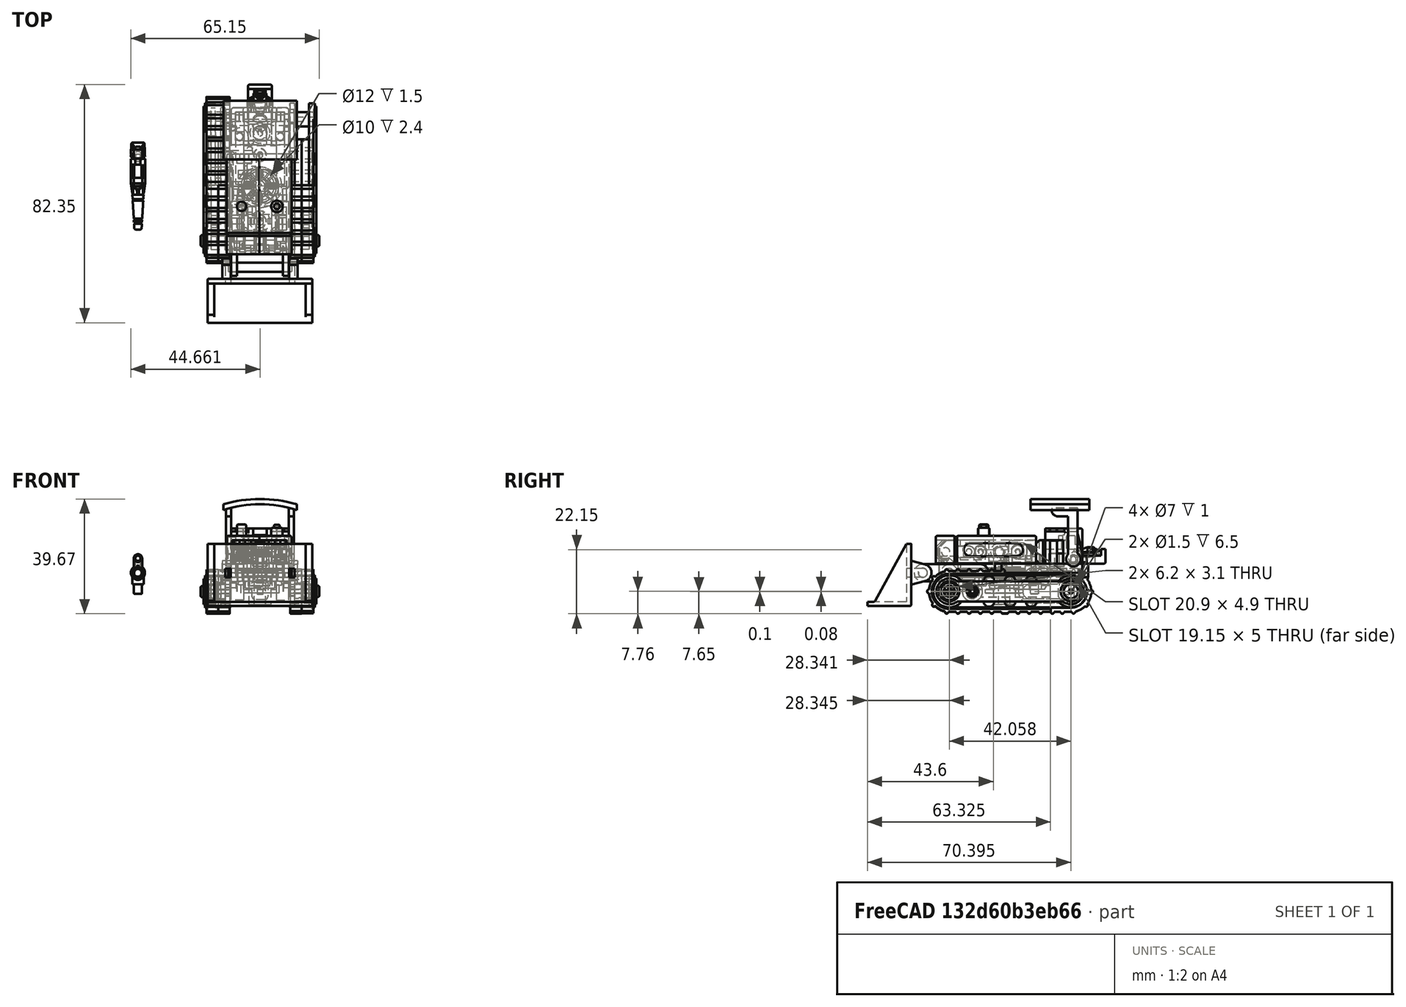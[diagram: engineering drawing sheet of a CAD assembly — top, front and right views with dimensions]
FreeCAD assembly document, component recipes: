
FREECAD ASSEMBLY — COMPONENT RECIPES ("Bonecrusher")

This assembly document has 22 components, labeled P0..P21 below (a component is one placed body or linked part). 22 of them carry a construction recipe — the FreeCAD feature program that regenerates the part from scratch, quoted from this document or its linked companion documents; the rest are supplied as boundary geometry only. No exploded tour is included for this assembly.
NOTE — document 3 of 4 of this assembly tour. The two overview renders and the header above are repeated from document 1; the component sections below continue where the previous document stopped.
COMPONENT P13 — recipe-attached ("Pre_Left_Outer_Leg", modeled in this document).
Construction recipe (the document's own serialized feature program — sketch geometry with constraints, then the solid features built on it; lengths are millimeters unless a unit is written):

FEATURE [Sketcher::SketchObject] Sketch286
  ArcFitTolerance = 1e-06
  AttachmentSupport = -> [XY_Plane026]
  FullyConstrained = true
  MakeInternals = false
  MapMode = 5
  sketch-geometry (4):
    g0: ArcOfCircle CenterX=0 CenterY=0 CenterZ=0 NormalX=0 NormalY=0 NormalZ=1 AngleXU=0 Radius=5.55 StartAngle=1.5708 EndAngle=4.71239
    g1: ArcOfCircle CenterX=42.05 CenterY=4e-16 CenterZ=0 NormalX=0 NormalY=0 NormalZ=1 AngleXU=0 Radius=5.55 StartAngle=4.71239 EndAngle=7.85398
    g2: LineSegment StartX=-3e-15 StartY=5.55 StartZ=0 EndX=42.05 EndY=5.55 EndZ=0
    g3: LineSegment StartX=-1e-15 StartY=-5.55 StartZ=0 EndX=42.05 EndY=-5.55 EndZ=0
  constraints (9):
    c: Tangent(g0,g2) = 1.5708
    c: Tangent(g0,g3) = -1.5708
    c: Tangent(g1,g2) = 1.5708
    c: Tangent(g1,g3) = -1.5708
    c: Equal(g0,g1)
    c: Horizontal(g3)
    c: Coincident(g0,g-1)
    c: DistanceX(g0,g1) = 42.05
    c: Diameter(g0) = 11.1
FEATURE [PartDesign::Pad] Pad164
  Direction = (0,0,1)
  Length = 1.6
  Length2 = 10
  Profile = -> Sketch286
  ReferenceAxis = -> Sketch286 [N_Axis]
  Refine = true
  Suppressed = false
  Type = 0
FEATURE [Sketcher::SketchObject] Sketch287
  ArcFitTolerance = 1e-06
  AttachmentSupport = -> [Pad164]
  ExternalGeometry = -> [Pad164]
  FullyConstrained = true
  MakeInternals = false
  MapMode = 5
  Placement = pos=(0,0,1.6) rot=(0,0,1;0rad)
  sketch-geometry (4):
    g0: ArcOfCircle CenterX=0 CenterY=0 CenterZ=0 NormalX=0 NormalY=0 NormalZ=1 AngleXU=0 Radius=3.5 StartAngle=1.5708 EndAngle=4.71239
    g1: ArcOfCircle CenterX=42.05 CenterY=4e-16 CenterZ=0 NormalX=0 NormalY=0 NormalZ=1 AngleXU=0 Radius=3.5 StartAngle=4.71239 EndAngle=7.85398
    g2: LineSegment StartX=-6e-16 StartY=3.5 StartZ=0 EndX=42.05 EndY=3.5 EndZ=0
    g3: LineSegment StartX=-6e-16 StartY=-3.5 StartZ=0 EndX=42.05 EndY=-3.5 EndZ=0
  constraints (8):
    c: Tangent(g0,g2) = 1.5708
    c: Tangent(g0,g3) = -1.5708
    c: Tangent(g1,g2) = 1.5708
    c: Tangent(g1,g3) = -1.5708
    c: Equal(g0,g1)
    c: Diameter(g0) = 7
    c: Coincident(g0,g-1)
    c: Coincident(g1,g-3)
FEATURE [PartDesign::Pad] Pad165
  BaseFeature = -> Pad164
  Direction = (0,0,1)
  Length = 1
  Length2 = 10
  Profile = -> Sketch287
  ReferenceAxis = -> Sketch287 [N_Axis]
  Refine = true
  Suppressed = false
  Type = 0
FEATURE [Sketcher::SketchObject] Sketch288
  ArcFitTolerance = 1e-06
  AttachmentSupport = -> [Pad165]
  ExternalGeometry = -> [Pad165]
  FullyConstrained = true
  MakeInternals = false
  MapMode = 5
  Placement = pos=(0,0,1.6) rot=(0,0,1;0rad)
  sketch-geometry (14):
    g0: Circle CenterX=42.05 CenterY=0 CenterZ=0 NormalX=0 NormalY=0 NormalZ=1 AngleXU=0 Radius=5.55
    g1: Circle CenterX=0 CenterY=0 CenterZ=0 NormalX=0 NormalY=0 NormalZ=1 AngleXU=0 Radius=5.55
    g2: ArcOfCircle CenterX=13.725 CenterY=3.5 CenterZ=0 NormalX=0 NormalY=0 NormalZ=1 AngleXU=0 Radius=1.85 StartAngle=1e-16 EndAngle=3.14159
    g3: ArcOfCircle CenterX=13.725 CenterY=-3.5 CenterZ=0 NormalX=0 NormalY=0 NormalZ=1 AngleXU=0 Radius=1.85 StartAngle=3.14159 EndAngle=6.28319
    g4: LineSegment StartX=15.575 StartY=3.5 StartZ=0 EndX=15.575 EndY=-3.5 EndZ=0
    g5: LineSegment StartX=11.875 StartY=3.5 StartZ=0 EndX=11.875 EndY=-3.5 EndZ=0
    g6: ArcOfCircle CenterX=21.025 CenterY=3.5 CenterZ=0 NormalX=0 NormalY=0 NormalZ=1 AngleXU=0 Radius=1.85 StartAngle=1e-16 EndAngle=3.14159
    g7: ArcOfCircle CenterX=21.025 CenterY=-3.5 CenterZ=0 NormalX=0 NormalY=0 NormalZ=1 AngleXU=0 Radius=1.85 StartAngle=3.14159 EndAngle=6.28319
    g8: LineSegment StartX=22.875 StartY=3.5 StartZ=0 EndX=22.875 EndY=-3.5 EndZ=0
    g9: LineSegment StartX=19.175 StartY=3.5 StartZ=0 EndX=19.175 EndY=-3.5 EndZ=0
    g10: ArcOfCircle CenterX=28.325 CenterY=3.5 CenterZ=0 NormalX=0 NormalY=0 NormalZ=1 AngleXU=0 Radius=1.85 StartAngle=1e-16 EndAngle=3.14159
    g11: ArcOfCircle CenterX=28.325 CenterY=-3.5 CenterZ=0 NormalX=0 NormalY=0 NormalZ=1 AngleXU=0 Radius=1.85 StartAngle=3.14159 EndAngle=6.28319
    g12: LineSegment StartX=30.175 StartY=3.5 StartZ=0 EndX=30.175 EndY=-3.5 EndZ=0
    g13: LineSegment StartX=26.475 StartY=3.5 StartZ=0 EndX=26.475 EndY=-3.5 EndZ=0
  constraints (33):
    c: Coincident(g0,g-3)
    c: PointOnObject(g-3,g0)
    c: Coincident(g1,g-1)
    c: Tangent(g2,g4) = 1.5708
    c: Tangent(g2,g5) = -1.5708
    c: Tangent(g3,g4) = 1.5708
    c: Tangent(g3,g5) = -1.5708
    c: Equal(g2,g3)
    c: Vertical(g5)
    c: PointOnObject(g2,g-5)
    c: PointOnObject(g3,g-4)
    c: Tangent(g6,g8) = 1.5708
    c: Tangent(g6,g9) = -1.5708
    c: Tangent(g7,g8) = 1.5708
    c: Tangent(g7,g9) = -1.5708
    c: Equal(g6,g7)
    c: Tangent(g10,g12) = 1.5708
    c: Tangent(g10,g13) = -1.5708
    c: Tangent(g11,g12) = 1.5708
    c: Tangent(g11,g13) = -1.5708
    c: Equal(g10,g11)
    c: Vertical(g13)
    c: PointOnObject(g10,g-5)
    c: PointOnObject(g11,g-4)
    c: Vertical(g8)
    c: PointOnObject(g7,g-4)
    c: Diameter(g1) = 11.1
    c: Diameter(g2) = 3.7
    c: Diameter(g6) = 3.7
    c: Diameter(g10) = 3.7
    c: DistanceX(g3,g7) = 3.6
    c: DistanceX(g7,g11) = 3.6
    c: Symmetric(g-5,g-5,g6)
FEATURE [PartDesign::Pad] Pad166
  BaseFeature = -> Pad165
  Direction = (0,0,1)
  Length = 0.5
  Length2 = 10
  Profile = -> Sketch288
  ReferenceAxis = -> Sketch288 [N_Axis]
  Refine = true
  Suppressed = false
  Type = 0
FEATURE [Sketcher::SketchObject] Sketch289
  ArcFitTolerance = 1e-06
  AttachmentSupport = -> [Pad166]
  ExternalGeometry = -> [Pad166]
  FullyConstrained = true
  MakeInternals = false
  MapMode = 5
  Placement = pos=(0,0,2.6) rot=(0,0,1;0rad)
  sketch-geometry (2):
    g0: Circle CenterX=0 CenterY=0 CenterZ=0 NormalX=0 NormalY=0 NormalZ=1 AngleXU=0 Radius=4.45
    g1: Circle CenterX=42.05 CenterY=0 CenterZ=0 NormalX=0 NormalY=0 NormalZ=1 AngleXU=0 Radius=4.45
  constraints (4):
    c: Coincident(g0,g-1)
    c: Coincident(g1,g-3)
    c: Diameter(g0) = 8.9
    c: Diameter(g1) = 8.9
FEATURE [PartDesign::Pad] Pad167
  BaseFeature = -> Pad166
  Direction = (0,0,1)
  Length = 1
  Length2 = 10
  Profile = -> Sketch289
  ReferenceAxis = -> Sketch289 [N_Axis]
  Refine = true
  Reversed = true
  Suppressed = false
  Type = 0
FEATURE [Sketcher::SketchObject] Sketch290
  ArcFitTolerance = 1e-06
  AttachmentSupport = -> [Pad167]
  ExternalGeometry = -> [Pad167]
  FullyConstrained = true
  MakeInternals = false
  MapMode = 5
  Placement = pos=(0,0,2.6) rot=(0,0,1;0rad)
  sketch-geometry (2):
    g0: Circle CenterX=42.05 CenterY=0 CenterZ=0 NormalX=0 NormalY=0 NormalZ=1 AngleXU=0 Radius=3.5
    g1: Circle CenterX=0 CenterY=0 CenterZ=0 NormalX=0 NormalY=0 NormalZ=1 AngleXU=0 Radius=3.5
  constraints (4):
    c: Coincident(g0,g-3)
    c: Coincident(g1,g-1)
    c: Diameter(g1) = 7
    c: Diameter(g0) = 7
FEATURE [PartDesign::Pocket] Pocket136
  BaseFeature = -> Pad167
  Direction = (0,0,-1)
  Length = 1
  Length2 = 5
  Profile = -> Sketch290
  ReferenceAxis = -> Sketch290 [N_Axis]
  Refine = true
  Suppressed = false
  Type = 0
FEATURE [Sketcher::SketchObject] Sketch291
  ArcFitTolerance = 1e-06
  AttachmentSupport = -> [Pocket136]
  ExternalGeometry = -> [Pocket136]
  FullyConstrained = true
  MakeInternals = false
  MapMode = 5
  Placement = pos=(0,0,1.6) rot=(0,0,1;0rad)
  sketch-geometry (1):
    g0: Circle CenterX=42.05 CenterY=0 CenterZ=0 NormalX=0 NormalY=0 NormalZ=1 AngleXU=0 Radius=2.5
  constraints (2):
    c: Coincident(g0,g-3)
    c: Diameter(g0) = 5
FEATURE [PartDesign::Pocket] Pocket137
  BaseFeature = -> Pocket136
  Direction = (0,0,-1)
  Length = 2
  Length2 = 5
  Profile = -> Sketch291
  ReferenceAxis = -> Sketch291 [N_Axis]
  Refine = true
  Suppressed = false
  Type = 0
FEATURE [Sketcher::SketchObject] Sketch292
  ArcFitTolerance = 1e-06
  AttachmentSupport = -> [Pocket137]
  FullyConstrained = true
  MakeInternals = false
  MapMode = 5
  Placement = pos=(0,0,1.6) rot=(0,0,1;0rad)
  sketch-geometry (1):
    g0: Circle CenterX=0 CenterY=0 CenterZ=0 NormalX=0 NormalY=0 NormalZ=1 AngleXU=0 Radius=3
  constraints (2):
    c: Coincident(g0,g-1)
    c: Diameter(g0) = 6
FEATURE [PartDesign::Pad] Pad168
  BaseFeature = -> Pocket137
  Direction = (0,0,1)
  Length = 1
  Length2 = 10
  Profile = -> Sketch292
  ReferenceAxis = -> Sketch292 [N_Axis]
  Refine = true
  Suppressed = false
  Type = 0
FEATURE [Sketcher::SketchObject] Sketch293
  ArcFitTolerance = 1e-06
  AttachmentSupport = -> [Pad168]
  FullyConstrained = true
  MakeInternals = false
  MapMode = 5
  Placement = pos=(0,0,2.6) rot=(0,0,1;0rad)
  sketch-geometry (1):
    g0: Circle CenterX=0 CenterY=0 CenterZ=0 NormalX=0 NormalY=0 NormalZ=1 AngleXU=0 Radius=1.95
  constraints (2):
    c: Coincident(g0,g-1)
    c: Diameter(g0) = 3.9
FEATURE [PartDesign::Pad] Pad169
  BaseFeature = -> Pad168
  Direction = (0,0,1)
  Length = 1
  Length2 = 10
  Profile = -> Sketch293
  ReferenceAxis = -> Sketch293 [N_Axis]
  Refine = true
  Suppressed = false
  Type = 0
FEATURE [PartDesign::Fillet] Fillet049
  Base = -> Pad169 [Edge90]
  BaseFeature = -> Pad169
  Radius = 0.5
  Refine = true
  SupportTransform = false
  Suppressed = false
  UseAllEdges = false
FEATURE [Sketcher::SketchObject] Sketch294
  ArcFitTolerance = 1e-06
  AttachmentSupport = -> [Fillet049]
  FullyConstrained = true
  MakeInternals = false
  MapMode = 5
  Placement = pos=(0,0,3.6) rot=(0,0,1;0rad)
  sketch-geometry (8):
    g0: ArcOfCircle CenterX=0 CenterY=1.25 CenterZ=0 NormalX=0 NormalY=0 NormalZ=1 AngleXU=0 Radius=0.375 StartAngle=4e-16 EndAngle=3.14159
    g1: ArcOfCircle CenterX=0 CenterY=-1.25 CenterZ=0 NormalX=0 NormalY=0 NormalZ=1 AngleXU=0 Radius=0.375 StartAngle=3.14159 EndAngle=6.28319
    g2: LineSegment StartX=0.375 StartY=1.25 StartZ=0 EndX=0.375 EndY=-1.25 EndZ=0
    g3: LineSegment StartX=-0.375 StartY=1.25 StartZ=0 EndX=-0.375 EndY=-1.25 EndZ=0
    g4: ArcOfCircle CenterX=-1.25 CenterY=0 CenterZ=0 NormalX=0 NormalY=0 NormalZ=1 AngleXU=0 Radius=0.375 StartAngle=1.5708 EndAngle=4.71239
    g5: ArcOfCircle CenterX=1.25 CenterY=0 CenterZ=0 NormalX=0 NormalY=0 NormalZ=1 AngleXU=0 Radius=0.375 StartAngle=4.71239 EndAngle=7.85398
    g6: LineSegment StartX=-1.25 StartY=0.375 StartZ=0 EndX=1.25 EndY=0.375 EndZ=0
    g7: LineSegment StartX=-1.25 StartY=-0.375 StartZ=0 EndX=1.25 EndY=-0.375 EndZ=0
  constraints (20):
    c: Tangent(g0,g2) = 1.5708
    c: Tangent(g0,g3) = -1.5708
    c: Tangent(g1,g2) = 1.5708
    c: Tangent(g1,g3) = -1.5708
    c: Equal(g0,g1)
    c: Vertical(g3)
    c: PointOnObject(g0,g-2)
    c: Tangent(g4,g6) = 1.5708
    c: Tangent(g4,g7) = -1.5708
    c: Tangent(g5,g6) = 1.5708
    c: Tangent(g5,g7) = -1.5708
    c: Equal(g4,g5)
    c: Horizontal(g7)
    c: Diameter(g0) = 0.75
    c: Diameter(g5) = 0.75
    c: PointOnObject(g5,g-1)
    c: DistanceX(g4,g-1) = 1.25
    c: DistanceX(g-1,g5) = 1.25
    c: DistanceY(g-1,g0) = 1.25
    c: DistanceY(g1,g-1) = 1.25
FEATURE [PartDesign::Pocket] Pocket138
  BaseFeature = -> Fillet049
  Direction = (0,0,-1)
  Length = 0.5
  Length2 = 5
  Profile = -> Sketch294
  ReferenceAxis = -> Sketch294 [N_Axis]
  Refine = true
  Suppressed = false
  Type = 0
FEATURE [Sketcher::SketchObject] Sketch295
  ArcFitTolerance = 1e-06
  AttachmentSupport = -> [Pocket138]
  ExternalGeometry = -> [Pocket138]
  FullyConstrained = true
  MakeInternals = false
  MapMode = 5
  Placement = pos=(0,0,1.6) rot=(0,0,1;0rad)
  sketch-geometry (6):
    g0: ArcOfCircle CenterX=0 CenterY=0 CenterZ=0 NormalX=0 NormalY=0 NormalZ=1 AngleXU=0 Radius=7.05 StartAngle=1.5708 EndAngle=4.71239
    g1: LineSegment StartX=4e-16 StartY=7.05 StartZ=0 EndX=35.05 EndY=7.05 EndZ=0
    g2: LineSegment StartX=-1.3e-15 StartY=-7.05 StartZ=0 EndX=19.175 EndY=-7.05 EndZ=0
    g3: LineSegment StartX=19.175 StartY=-7.05 StartZ=0 EndX=19.175 EndY=0 EndZ=0
    g4: LineSegment StartX=35.05 StartY=7.05 StartZ=0 EndX=35.05 EndY=0 EndZ=0
    g5: LineSegment StartX=35.05 StartY=0 StartZ=0 EndX=19.175 EndY=0 EndZ=0
  constraints (17):
    c: PointOnObject(g0,g-2)
    c: PointOnObject(g0,g-2)
    c: Coincident(g0,g-1)
    c: Diameter(g0) = 14.1
    c: Coincident(g1,g0)
    c: Horizontal(g1)
    c: DistanceX(g1,g-4) = 7
    c: Tangent(g2,g0) = -1.5708
    c: DistanceX(g-6,g2) = 0
    c: Coincident(g3,g2)
    c: PointOnObject(g3,g-1)
    c: Vertical(g3)
    c: PointOnObject(g4,g-1)
    c: Vertical(g4)
    c: Coincident(g5,g4)
    c: Coincident(g5,g3)
    c: Coincident(g4,g1)
FEATURE [PartDesign::Pad] Pad170
  BaseFeature = -> Pocket138
  Direction = (0,0,1)
  Length = 4.05
  Length2 = 10
  Profile = -> Sketch295
  ReferenceAxis = -> Sketch295 [N_Axis]
  Refine = true
  Reversed = true
  Suppressed = false
  Type = 0
FEATURE [Sketcher::SketchObject] Sketch296
  ArcFitTolerance = 1e-06
  AttachmentSupport = -> [Pad170]
  ExternalGeometry = -> [Pad170]
  FullyConstrained = true
  MakeInternals = false
  MapMode = 5
  Placement = pos=(0,0,1.6) rot=(0,0,1;0rad)
  sketch-geometry (8):
    g0: ArcOfCircle CenterX=0 CenterY=1e-16 CenterZ=0 NormalX=0 NormalY=0 NormalZ=1 AngleXU=0 Radius=5.55 StartAngle=1.5708 EndAngle=4.71239
    g1: LineSegment StartX=-1e-15 StartY=-5.55 StartZ=0 EndX=19.175 EndY=-5.55 EndZ=0
    g2: LineSegment StartX=-1.08e-14 StartY=5.55 StartZ=0 EndX=35.05 EndY=5.55 EndZ=0
    g3: ArcOfCircle CenterX=0 CenterY=1e-16 CenterZ=0 NormalX=0 NormalY=0 NormalZ=1 AngleXU=0 Radius=6.05 StartAngle=1.5708 EndAngle=4.71239
    g4: LineSegment StartX=4e-16 StartY=6.05 StartZ=0 EndX=35.05 EndY=6.05 EndZ=0
    g5: LineSegment StartX=35.05 StartY=6.05 StartZ=0 EndX=35.05 EndY=5.55 EndZ=0
    g6: LineSegment StartX=-1.1e-15 StartY=-6.05 StartZ=0 EndX=19.175 EndY=-6.05 EndZ=0
    g7: LineSegment StartX=19.175 StartY=-6.05 StartZ=0 EndX=19.175 EndY=-5.55 EndZ=0
  constraints (21):
    c: Coincident(g0,g-3)
    c: Tangent(g1,g0) = -1.5708
    c: Coincident(g1,g-4)
    c: Coincident(g2,g0)
    c: Coincident(g2,g-5)
    c: Diameter(g-3) = 11.1
    c: PointOnObject(g3,g-2)
    c: PointOnObject(g3,g-2)
    c: Diameter(g3) = 12.1
    c: Coincident(g3,g0)
    c: Coincident(g5,g4)
    c: Coincident(g5,g2)
    c: Vertical(g5)
    c: Tangent(g6,g3) = -1.5708
    c: PointOnObject(g6,g-4)
    c: Horizontal(g6)
    c: Coincident(g7,g6)
    c: Coincident(g7,g1)
    c: Horizontal(g1)
    c: Horizontal(g4)
    c: Coincident(g4,g3)
FEATURE [PartDesign::Pocket] Pocket139
  BaseFeature = -> Pad170
  Direction = (0,0,-1)
  Length = 0.5
  Length2 = 5
  Profile = -> Sketch296
  ReferenceAxis = -> Sketch296 [N_Axis]
  Refine = true
  Suppressed = false
  Type = 0
FEATURE [Sketcher::SketchObject] Sketch297
  ArcFitTolerance = 1e-06
  AttachmentSupport = -> [Pocket139]
  ExternalGeometry = -> [Pocket139]
  FullyConstrained = true
  MakeInternals = false
  MapMode = 5
  Placement = pos=(0,0,-2.45) rot=(1,0,0;3.14159rad)
  sketch-geometry (6):
    g0: LineSegment StartX=19.175 StartY=5.55 StartZ=0 EndX=0 EndY=5.55 EndZ=0
    g1: LineSegment StartX=35.05 StartY=-5.55 StartZ=0 EndX=0 EndY=-5.55 EndZ=0
    g2: ArcOfCircle CenterX=0 CenterY=0 CenterZ=0 NormalX=0 NormalY=0 NormalZ=1 AngleXU=0 Radius=5.55 StartAngle=1.5708 EndAngle=4.71239
    g3: LineSegment StartX=35.05 StartY=-5.55 StartZ=0 EndX=35.05 EndY=0 EndZ=0
    g4: LineSegment StartX=35.05 StartY=0 StartZ=0 EndX=19.175 EndY=0 EndZ=0
    g5: LineSegment StartX=19.175 StartY=0 StartZ=0 EndX=19.175 EndY=5.55 EndZ=0
  constraints (16):
    c: PointOnObject(g0,g-3)
    c: PointOnObject(g0,g-2)
    c: Horizontal(g0)
    c: PointOnObject(g1,g-4)
    c: PointOnObject(g1,g-2)
    c: Horizontal(g1)
    c: Coincident(g2,g0)
    c: Coincident(g2,g1)
    c: DistanceY(g0,g-3) = 1.5
    c: Coincident(g2,g-1)
    c: Coincident(g3,g1)
    c: Coincident(g3,g-4)
    c: Coincident(g4,g3)
    c: Coincident(g4,g-3)
    c: Coincident(g5,g4)
    c: Coincident(g5,g0)
FEATURE [PartDesign::Pocket] Pocket140
  BaseFeature = -> Pocket139
  Direction = (0,0,1)
  Length = 2.45
  Length2 = 5
  Profile = -> Sketch297
  ReferenceAxis = -> Sketch297 [N_Axis]
  Refine = true
  Suppressed = false
  Type = 0
FEATURE [Sketcher::SketchObject] Sketch298
  ArcFitTolerance = 1e-06
  AttachmentSupport = -> [Pocket140]
  ExternalGeometry = -> [Pocket140]
  FullyConstrained = true
  MakeInternals = false
  MapMode = 5
  Placement = pos=(0,0,1.6) rot=(0,0,1;0rad)
  sketch-geometry (38):
    g0: ArcOfCircle CenterX=18.575 CenterY=-7.05 CenterZ=0 NormalX=0 NormalY=0 NormalZ=1 AngleXU=0 Radius=0.6 StartAngle=3.14159 EndAngle=6.28319
    g1: ArcOfCircle CenterX=14.675 CenterY=-7.05 CenterZ=0 NormalX=0 NormalY=0 NormalZ=1 AngleXU=0 Radius=0.6 StartAngle=3.14159 EndAngle=6.28319
    g2: ArcOfCircle CenterX=10.775 CenterY=-7.05 CenterZ=0 NormalX=0 NormalY=0 NormalZ=1 AngleXU=0 Radius=0.6 StartAngle=3.14159 EndAngle=6.28319
    g3: ArcOfCircle CenterX=6.875 CenterY=-7.05 CenterZ=0 NormalX=0 NormalY=0 NormalZ=1 AngleXU=0 Radius=0.6 StartAngle=3.14159 EndAngle=6.28319
    g4: ArcOfCircle CenterX=2.975 CenterY=-7.05 CenterZ=0 NormalX=0 NormalY=0 NormalZ=1 AngleXU=0 Radius=0.6 StartAngle=3.14159 EndAngle=6.28319
    g5: ArcOfCircle CenterX=-7.05 CenterY=0 CenterZ=0 NormalX=0 NormalY=0 NormalZ=1 AngleXU=0 Radius=0.6 StartAngle=1.52823 EndAngle=4.75496
    g6: ArcOfCircle CenterX=-0.922632 CenterY=-6.98937 CenterZ=0 NormalX=0 NormalY=0 NormalZ=1 AngleXU=0 Radius=0.6 StartAngle=2.96778 EndAngle=6.19451
    g7: ArcOfCircle CenterX=-5.30094 CenterY=-4.64785 CenterZ=0 NormalX=0 NormalY=0 NormalZ=1 AngleXU=0 Radius=0.6 StartAngle=2.24808 EndAngle=5.4748
    g8: ArcOfCircle CenterX=-5.30161 CenterY=4.64708 CenterZ=0 NormalX=0 NormalY=0 NormalZ=1 AngleXU=0 Radius=0.6 StartAngle=0.808528 EndAngle=4.03525
    g9: ArcOfCircle CenterX=-0.923647 CenterY=6.98923 CenterZ=0 NormalX=0 NormalY=0 NormalZ=1 AngleXU=0 Radius=0.6 StartAngle=0.0888255 EndAngle=3.31555
    g10: ArcOfCircle CenterX=2.97399 CenterY=7.05 CenterZ=0 NormalX=0 NormalY=0 NormalZ=1 AngleXU=0 Radius=0.6 StartAngle=0 EndAngle=3.14159
    g11: ArcOfCircle CenterX=6.87399 CenterY=7.05 CenterZ=0 NormalX=0 NormalY=0 NormalZ=1 AngleXU=0 Radius=0.6 StartAngle=0 EndAngle=3.14159
    g12: ArcOfCircle CenterX=10.774 CenterY=7.05 CenterZ=0 NormalX=0 NormalY=0 NormalZ=1 AngleXU=0 Radius=0.6 StartAngle=5e-16 EndAngle=3.14159
    g13: ArcOfCircle CenterX=14.674 CenterY=7.05 CenterZ=0 NormalX=0 NormalY=0 NormalZ=1 AngleXU=0 Radius=0.6 StartAngle=0 EndAngle=3.14159
    g14: ArcOfCircle CenterX=18.574 CenterY=7.05 CenterZ=0 NormalX=0 NormalY=0 NormalZ=1 AngleXU=0 Radius=0.6 StartAngle=1.5708 EndAngle=3.14159
    g15: ArcOfCircle CenterX=19.874 CenterY=7.05 CenterZ=0 NormalX=0 NormalY=0 NormalZ=1 AngleXU=0 Radius=0.6 StartAngle=6e-16 EndAngle=1.5708
    g16: LineSegment StartX=19.874 StartY=7.65 StartZ=0 EndX=18.574 EndY=7.65 EndZ=0
    g17: ArcOfCircle CenterX=23.774 CenterY=7.05 CenterZ=0 NormalX=0 NormalY=0 NormalZ=1 AngleXU=0 Radius=0.6 StartAngle=5e-16 EndAngle=3.14159
    g18: ArcOfCircle CenterX=27.674 CenterY=7.05 CenterZ=0 NormalX=0 NormalY=0 NormalZ=1 AngleXU=0 Radius=0.6 StartAngle=1e-16 EndAngle=3.14159
    g19: ArcOfCircle CenterX=31.574 CenterY=7.05 CenterZ=0 NormalX=0 NormalY=0 NormalZ=1 AngleXU=0 Radius=0.6 StartAngle=2e-16 EndAngle=3.14159
    g20: LineSegment StartX=32.174 StartY=7.05 StartZ=0 EndX=30.974 EndY=7.05 EndZ=0
    g21: LineSegment StartX=28.274 StartY=7.05 StartZ=0 EndX=27.074 EndY=7.05 EndZ=0
    g22: LineSegment StartX=24.374 StartY=7.05 StartZ=0 EndX=23.174 EndY=7.05 EndZ=0
    g23: LineSegment StartX=20.474 StartY=7.05 StartZ=0 EndX=17.974 EndY=7.05 EndZ=0
    g24: LineSegment StartX=15.274 StartY=7.05 StartZ=0 EndX=14.074 EndY=7.05 EndZ=0
    g25: LineSegment StartX=11.374 StartY=7.05 StartZ=0 EndX=10.174 EndY=7.05 EndZ=0
    g26: LineSegment StartX=7.47399 StartY=7.05 StartZ=0 EndX=6.27399 EndY=7.05 EndZ=0
    g27: LineSegment StartX=3.57399 StartY=7.05 StartZ=0 EndX=2.37399 EndY=7.05 EndZ=0
    g28: LineSegment StartX=-0.326013 StartY=7.04246 StartZ=0 EndX=-1.51459 EndY=6.88538 EndZ=0
    g29: LineSegment StartX=-4.88728 StartY=5.08105 StartZ=0 EndX=-5.67755 EndY=4.17946 EndZ=0
    g30: LineSegment StartX=-7.02447 StartY=0.599457 StartZ=0 EndX=-7.02447 EndY=-0.599457 EndZ=0
    g31: LineSegment StartX=-5.67694 StartY=-4.18029 StartZ=0 EndX=-4.88654 EndY=-5.08176 EndZ=0
    g32: LineSegment StartX=-0.32499 StartY=-7.04251 StartZ=0 EndX=-1.51359 EndY=-6.8856 EndZ=0
    g33: LineSegment StartX=2.375 StartY=-7.05 StartZ=0 EndX=3.575 EndY=-7.05 EndZ=0
    g34: LineSegment StartX=6.275 StartY=-7.05 StartZ=0 EndX=7.475 EndY=-7.05 EndZ=0
    g35: LineSegment StartX=10.175 StartY=-7.05 StartZ=0 EndX=11.375 EndY=-7.05 EndZ=0
    g36: LineSegment StartX=14.075 StartY=-7.05 StartZ=0 EndX=15.275 EndY=-7.05 EndZ=0
    g37: LineSegment StartX=17.975 StartY=-7.05 StartZ=0 EndX=19.175 EndY=-7.05 EndZ=0
  constraints (132):
    c: Coincident(g0,g-3)
    c: PointOnObject(g0,g-3)
    c: PointOnObject(g1,g-3)
    c: PointOnObject(g1,g-3)
    c: PointOnObject(g2,g-3)
    c: PointOnObject(g2,g-3)
    c: PointOnObject(g3,g-3)
    c: PointOnObject(g3,g-3)
    c: PointOnObject(g4,g-3)
    c: PointOnObject(g4,g-3)
    c: Radius(g4) = 0.6
    c: Radius(g3) = 0.6
    c: Radius(g2) = 0.6
    c: Radius(g1) = 0.6
    c: Radius(g0) = 0.6
    c: DistanceX(g1,g0) = 2.7
    c: PointOnObject(g4,g-3)
    c: PointOnObject(g3,g-3)
    c: PointOnObject(g2,g-3)
    c: PointOnObject(g1,g-3)
    c: PointOnObject(g0,g-3)
    c: DistanceX(g2,g1) = 2.7
    c: DistanceX(g3,g2) = 2.7
    c: DistanceX(g4,g3) = 2.7
    c: PointOnObject(g5,g-4)
    c: PointOnObject(g5,g-4)
    c: PointOnObject(g6,g-4)
    c: PointOnObject(g6,g-4)
    c: PointOnObject(g7,g-4)
    c: PointOnObject(g7,g-4)
    c: Distance(g4,g6) = 2.7
    c: Radius(g6) = 0.6
    c: Radius(g7) = 0.6
    c: Radius(g5) = 0.6
    c: PointOnObject(g5,g-4)
    c: PointOnObject(g5,g-1)
    c: PointOnObject(g6,g-4)
    c: PointOnObject(g7,g-4)
    c: Distance(g6,g7) = 3.825
    c: PointOnObject(g8,g-4)
    c: PointOnObject(g8,g-4)
    c: PointOnObject(g9,g-4)
    c: PointOnObject(g9,g-4)
    c: Radius(g8) = 0.6
    c: Radius(g9) = 0.6
    c: Radius(g10) = 0.6
    c: Radius(g11) = 0.6
    c: Radius(g12) = 0.6
    c: PointOnObject(g9,g-4)
    c: PointOnObject(g8,g-4)
    c: Distance(g5,g8) = 3.825
    c: Distance(g8,g9) = 3.825
    c: DistanceX(g9,g10) = 2.7
    c: DistanceX(g10,g11) = 2.7
    c: DistanceX(g11,g12) = 2.7
    c: Radius(g13) = 0.6
    c: DistanceX(g12,g13) = 2.7
    c: Coincident(g16,g15)
    c: Coincident(g16,g14)
    c: Horizontal(g16)
    c: Radius(g14) = 0.6
    c: Radius(g15) = 0.6
    c: DistanceX(g15,g15) = 0
    c: DistanceX(g14,g14) = 0
    c: DistanceX(g13,g14) = 2.7
    c: PointOnObject(g13,g-5)
    c: PointOnObject(g12,g-5)
    c: PointOnObject(g11,g-5)
    c: PointOnObject(g10,g-5)
    c: PointOnObject(g12,g-5)
    c: PointOnObject(g12,g-5)
    c: PointOnObject(g10,g-5)
    c: PointOnObject(g10,g-5)
    c: PointOnObject(g11,g-5)
    c: PointOnObject(g11,g-5)
    c: PointOnObject(g13,g-5)
    c: PointOnObject(g13,g-5)
    c: PointOnObject(g14,g-5)
    c: PointOnObject(g14,g-5)
    c: PointOnObject(g15,g-5)
    c: DistanceX(g14,g15) = 2.5
    c: PointOnObject(g17,g-5)
    c: PointOnObject(g17,g-5)
    c: PointOnObject(g18,g-5)
    c: PointOnObject(g18,g-5)
    c: PointOnObject(g19,g-5)
    c: PointOnObject(g19,g-5)
    c: Radius(g17) = 0.6
    c: Radius(g18) = 0.6
    c: Radius(g19) = 0.6
    c: DistanceX(g15,g17) = 2.7
    c: DistanceX(g17,g18) = 2.7
    c: DistanceX(g18,g19) = 2.7
    c: PointOnObject(g19,g-5)
    c: PointOnObject(g18,g-5)
    c: PointOnObject(g17,g-5)
    c: Coincident(g20,g19)
    c: Coincident(g20,g19)
    c: Coincident(g21,g18)
    c: Coincident(g21,g18)
    c: Coincident(g22,g17)
    c: Coincident(g22,g17)
    c: Coincident(g23,g15)
    c: Coincident(g23,g14)
    c: Coincident(g24,g13)
    c: Coincident(g24,g13)
    c: Coincident(g25,g12)
    c: Coincident(g25,g12)
    c: Coincident(g26,g11)
    c: Coincident(g26,g11)
    c: Coincident(g27,g10)
    c: Coincident(g27,g10)
    c: Coincident(g28,g9)
    c: Coincident(g28,g9)
    c: Coincident(g29,g8)
    c: Coincident(g29,g8)
    c: Coincident(g30,g5)
    c: Coincident(g30,g5)
    c: Coincident(g31,g7)
    c: Coincident(g31,g7)
    c: Coincident(g32,g6)
    c: Coincident(g32,g6)
    c: Coincident(g33,g4)
    c: Coincident(g33,g4)
    c: Coincident(g34,g3)
    c: Coincident(g34,g3)
    c: Coincident(g35,g2)
    c: Coincident(g35,g2)
    c: Coincident(g36,g1)
    c: Coincident(g36,g1)
    c: Coincident(g37,g0)
    c: Coincident(g37,g0)
FEATURE [PartDesign::Pad] Pad171
  BaseFeature = -> Pocket140
  Direction = (0,0,1)
  Length = 4.05
  Length2 = 10
  Profile = -> Sketch298
  ReferenceAxis = -> Sketch298 [N_Axis]
  Refine = true
  Reversed = true
  Suppressed = false
  Type = 0
FEATURE [Sketcher::SketchObject] Sketch299
  ArcFitTolerance = 1e-06
  AttachmentSupport = -> [Pad171]
  ExternalGeometry = -> [Pad171]
  FullyConstrained = true
  MakeInternals = false
  MapMode = 5
  Placement = pos=(0,0,3e-16) rot=(1,0,0;3.14159rad)
  sketch-geometry (8):
    g0: LineSegment StartX=-3 StartY=2.35 StartZ=0 EndX=-3 EndY=-2.35 EndZ=0
    g1: LineSegment StartX=-3 StartY=-2.35 StartZ=0 EndX=-1.6 EndY=-2.35 EndZ=0
    g2: LineSegment StartX=-1.6 StartY=-2.35 StartZ=0 EndX=-1.6 EndY=2.35 EndZ=0
    g3: LineSegment StartX=-1.6 StartY=2.35 StartZ=0 EndX=-3 EndY=2.35 EndZ=0
    g4: LineSegment StartX=1.6 StartY=2.35 StartZ=0 EndX=1.6 EndY=-2.35 EndZ=0
    g5: LineSegment StartX=1.6 StartY=-2.35 StartZ=0 EndX=3 EndY=-2.35 EndZ=0
    g6: LineSegment StartX=3 StartY=-2.35 StartZ=0 EndX=3 EndY=2.35 EndZ=0
    g7: LineSegment StartX=3 StartY=2.35 StartZ=0 EndX=1.6 EndY=2.35 EndZ=0
  constraints (24):
    c: Coincident(g0,g1)
    c: Coincident(g1,g2)
    c: Coincident(g2,g3)
    c: Coincident(g3,g0)
    c: Vertical(g0)
    c: Vertical(g2)
    c: Horizontal(g1)
    c: Horizontal(g3)
    c: Coincident(g4,g5)
    c: Coincident(g5,g6)
    c: Coincident(g6,g7)
    c: Coincident(g7,g4)
    c: Vertical(g4)
    c: Vertical(g6)
    c: Horizontal(g5)
    c: Horizontal(g7)
    c: DistanceY(g0,g0) = 4.7
    c: DistanceY(g4,g4) = 4.7
    c: DistanceX(g3,g3) = 1.4
    c: DistanceX(g7,g7) = 1.4
    c: DistanceY(g4,g-3) = 3.2
    c: DistanceY(g2,g-3) = 3.2
    c: DistanceX(g1,g4) = 3.2
    c: DistanceX(g2,g-1) = 1.6
FEATURE [PartDesign::Pad] Pad172
  BaseFeature = -> Pad171
  Direction = (0,0,-1)
  Length = 4.9
  Length2 = 10
  Profile = -> Sketch299
  ReferenceAxis = -> Sketch299 [N_Axis]
  Refine = true
  Suppressed = false
  Type = 0
FEATURE [Sketcher::SketchObject] Sketch300
  ArcFitTolerance = 1e-06
  AttachmentSupport = -> [Pad172]
  ExternalGeometry = -> [Pad172]
  FullyConstrained = true
  MakeInternals = false
  MapMode = 5
  Placement = pos=(0,0,-4.9) rot=(1,0,0;3.14159rad)
  sketch-geometry (8):
    g0: LineSegment StartX=-3 StartY=1.45 StartZ=0 EndX=-3 EndY=-1.45 EndZ=0
    g1: LineSegment StartX=-3 StartY=-1.45 StartZ=0 EndX=-1.6 EndY=-1.45 EndZ=0
    g2: LineSegment StartX=-1.6 StartY=-1.45 StartZ=0 EndX=-1.6 EndY=1.45 EndZ=0
    g3: LineSegment StartX=-1.6 StartY=1.45 StartZ=0 EndX=-3 EndY=1.45 EndZ=0
    g4: LineSegment StartX=1.6 StartY=1.45 StartZ=0 EndX=1.6 EndY=-1.45 EndZ=0
    g5: LineSegment StartX=1.6 StartY=-1.45 StartZ=0 EndX=3 EndY=-1.45 EndZ=0
    g6: LineSegment StartX=3 StartY=-1.45 StartZ=0 EndX=3 EndY=1.45 EndZ=0
    g7: LineSegment StartX=3 StartY=1.45 StartZ=0 EndX=1.6 EndY=1.45 EndZ=0
  constraints (24):
    c: Coincident(g0,g1)
    c: Coincident(g1,g2)
    c: Coincident(g2,g3)
    c: Coincident(g3,g0)
    c: Vertical(g0)
    c: Vertical(g2)
    c: Horizontal(g1)
    c: Horizontal(g3)
    c: PointOnObject(g0,g-3)
    c: PointOnObject(g1,g-4)
    c: Coincident(g4,g5)
    c: Coincident(g5,g6)
    c: Coincident(g6,g7)
    c: Coincident(g7,g4)
    c: Vertical(g4)
    c: Vertical(g6)
    c: Horizontal(g5)
    c: Horizontal(g7)
    c: PointOnObject(g4,g-5)
    c: PointOnObject(g5,g-6)
    c: DistanceY(g4,g4) = 2.9
    c: DistanceY(g0,g0) = 2.9
    c: DistanceY(g0,g-3) = 0.9
    c: DistanceY(g4,g-5) = 0.9
FEATURE [PartDesign::Pad] Pad173
  BaseFeature = -> Pad172
  Direction = (0,0,-1)
  Length = 1.6
  Length2 = 10
  Profile = -> Sketch300
  ReferenceAxis = -> Sketch300 [N_Axis]
  Refine = true
  Suppressed = false
  Type = 0
FEATURE [Sketcher::SketchObject] Sketch301
  ArcFitTolerance = 1e-06
  AttachmentSupport = -> [Pad173]
  FullyConstrained = true
  MakeInternals = false
  MapMode = 5
  Placement = pos=(0,0,3e-16) rot=(1,0,0;3.14159rad)
  sketch-geometry (1):
    g0: Circle CenterX=8 CenterY=0 CenterZ=0 NormalX=0 NormalY=0 NormalZ=1 AngleXU=0 Radius=3.5
  constraints (3):
    c: PointOnObject(g0,g-1)
    c: Diameter(g0) = 7
    c: DistanceX(g-1,g0) = 8
FEATURE [PartDesign::Pad] Pad174
  BaseFeature = -> Pad173
  Direction = (0,0,-1)
  Length = 2
  Length2 = 10
  Profile = -> Sketch301
  ReferenceAxis = -> Sketch301 [N_Axis]
  Refine = true
  Suppressed = false
  Type = 0
FEATURE [Sketcher::SketchObject] Sketch302
  ArcFitTolerance = 1e-06
  AttachmentSupport = -> [Pad174]
  ExternalGeometry = -> [Pad174]
  FullyConstrained = true
  MakeInternals = false
  MapMode = 5
  Placement = pos=(0,0,-2) rot=(1,0,0;3.14159rad)
  sketch-geometry (1):
    g0: Circle CenterX=8 CenterY=0 CenterZ=0 NormalX=0 NormalY=0 NormalZ=1 AngleXU=0 Radius=2.45
  constraints (2):
    c: Coincident(g0,g-3)
    c: Diameter(g0) = 4.9
FEATURE [PartDesign::Pocket] Pocket141
  BaseFeature = -> Pad174
  Direction = (0,0,1)
  Length = 2
  Length2 = 5
  Profile = -> Sketch302
  ReferenceAxis = -> Sketch302 [N_Axis]
  Refine = true
  Suppressed = false
  Type = 0
FEATURE [Sketcher::SketchObject] Sketch303
  ArcFitTolerance = 1e-06
  AttachmentSupport = -> [Pocket141]
  ExternalGeometry = -> [Pocket141]
  FullyConstrained = true
  MakeInternals = false
  MapMode = 5
  Placement = pos=(0,0,3e-16) rot=(1,0,0;3.14159rad)
  sketch-geometry (4):
    g0: LineSegment StartX=34.8723 StartY=2 StartZ=0 EndX=34.8723 EndY=-2 EndZ=0
    g1: LineSegment StartX=34.8723 StartY=2 StartZ=0 EndX=10.8723 EndY=2 EndZ=0
    g2: LineSegment StartX=34.8723 StartY=-2 StartZ=0 EndX=10.8723 EndY=-2 EndZ=0
    g3: ArcOfCircle CenterX=8 CenterY=0 CenterZ=0 NormalX=0 NormalY=0 NormalZ=1 AngleXU=0 Radius=3.5 StartAngle=5.67494 EndAngle=6.89143
  constraints (12):
    c: Vertical(g0)
    c: Coincident(g1,g0)
    c: PointOnObject(g1,g-3)
    c: Horizontal(g1)
    c: DistanceY(g-3,g0) = 2
    c: DistanceY(g0,g-3) = 2
    c: Coincident(g2,g0)
    c: Coincident(g3,g2)
    c: Coincident(g3,g1)
    c: Coincident(g3,g-3)
    c: DistanceX(g1,g1) = 24
    c: Horizontal(g2)
FEATURE [PartDesign::Pocket] Pocket142
  BaseFeature = -> Pocket141
  Direction = (0,0,1)
  Length = 1
  Length2 = 5
  Profile = -> Sketch303
  ReferenceAxis = -> Sketch303 [N_Axis]
  Refine = true
  Suppressed = false
  Type = 0
FEATURE [Sketcher::SketchObject] Sketch304
  ArcFitTolerance = 1e-06
  AttachmentSupport = -> [Pocket142]
  ExternalGeometry = -> [Pocket142]
  FullyConstrained = true
  MakeInternals = false
  MapMode = 5
  Placement = pos=(0,0,2e-16) rot=(1,0,0;3.14159rad)
  sketch-geometry (1):
    g0: Circle CenterX=8 CenterY=0 CenterZ=0 NormalX=0 NormalY=0 NormalZ=1 AngleXU=0 Radius=1.25
  constraints (2):
    c: Diameter(g0) = 2.5
    c: Coincident(g0,g-4)
FEATURE [PartDesign::Pocket] Pocket143
  BaseFeature = -> Pocket142
  Direction = (0,0,1)
  Length = 2.6
  Length2 = 5
  Profile = -> Sketch304
  ReferenceAxis = -> Sketch304 [N_Axis]
  Refine = true
  Suppressed = false
  Type = 0
FEATURE [Sketcher::SketchObject] Sketch305
  ArcFitTolerance = 1e-06
  AttachmentSupport = -> [Pocket143]
  ExternalGeometry = -> [Pocket143]
  FullyConstrained = true
  MakeInternals = false
  MapMode = 5
  Placement = pos=(0,0,2.6) rot=(0,0,1;0rad)
  sketch-geometry (1):
    g0: Circle CenterX=8 CenterY=0 CenterZ=0 NormalX=0 NormalY=0 NormalZ=1 AngleXU=0 Radius=1.95
  constraints (2):
    c: Diameter(g0) = 3.9
    c: Coincident(g0,g-4)
FEATURE [PartDesign::Pocket] Pocket144
  BaseFeature = -> Pocket143
  Direction = (0,0,-1)
  Length = 1.8
  Length2 = 5
  Profile = -> Sketch305
  ReferenceAxis = -> Sketch305 [N_Axis]
  Refine = true
  Suppressed = false
  Type = 0
FEATURE [Sketcher::SketchObject] Sketch306
  ArcFitTolerance = 1e-06
  AttachmentSupport = -> [Pocket144]
  ExternalGeometry = -> [Pocket144]
  FullyConstrained = true
  MakeInternals = false
  MapMode = 5
  Placement = pos=(0,0,-6.5) rot=(1,0,0;3.14159rad)
  sketch-geometry (8):
    g0: LineSegment StartX=-3 StartY=1.45 StartZ=0 EndX=-3 EndY=-1.45 EndZ=0
    g1: LineSegment StartX=-3 StartY=-1.45 StartZ=0 EndX=-1.6 EndY=-1.45 EndZ=0
    g2: LineSegment StartX=-1.6 StartY=-1.45 StartZ=0 EndX=-1.6 EndY=1.45 EndZ=0
    g3: LineSegment StartX=-1.6 StartY=1.45 StartZ=0 EndX=-3 EndY=1.45 EndZ=0
    g4: LineSegment StartX=1.6 StartY=1.45 StartZ=0 EndX=1.6 EndY=-1.45 EndZ=0
    g5: LineSegment StartX=1.6 StartY=-1.45 StartZ=0 EndX=3 EndY=-1.45 EndZ=0
    g6: LineSegment StartX=3 StartY=-1.45 StartZ=0 EndX=3 EndY=1.45 EndZ=0
    g7: LineSegment StartX=3 StartY=1.45 StartZ=0 EndX=1.6 EndY=1.45 EndZ=0
  constraints (20):
    c: Coincident(g0,g1)
    c: Coincident(g1,g2)
    c: Coincident(g2,g3)
    c: Coincident(g3,g0)
    c: Vertical(g0)
    c: Vertical(g2)
    c: Horizontal(g1)
    c: Horizontal(g3)
    c: Coincident(g0,g-3)
    c: Coincident(g1,g-4)
    c: Coincident(g4,g5)
    c: Coincident(g5,g6)
    c: Coincident(g6,g7)
    c: Coincident(g7,g4)
    c: Vertical(g4)
    c: Vertical(g6)
    c: Horizontal(g5)
    c: Horizontal(g7)
    c: Coincident(g4,g-5)
    c: Coincident(g5,g-6)
FEATURE [PartDesign::Pad] Pad175
  BaseFeature = -> Pocket144
  Direction = (0,0,-1)
  Length = 0.33
  Length2 = 10
  Profile = -> Sketch306
  ReferenceAxis = -> Sketch306 [N_Axis]
  Refine = true
  Suppressed = false
  Type = 0
FEATURE [PartDesign::Body] Body024  label="Pre_Left_Outer_Leg"
  AllowCompound = false
  Group = -> [Sketch286,Pad164,Sketch287,Pad165,Sketch288,Pad166,Sketch289,Pad167,Sketch290,Pocket136,Sketch291,Pocket137,Sketch292,Pad168,Sketch293,Pad169,Fillet049,Sketch294,Pocket138,Sketch295,Pad170,Sketch296,Pocket139,Sketch297,Pocket140,Sketch298,Pad171,Sketch299,Pad172,Sketch300,Pad173,Sketch301,Pad174,Sketch302,Pocket141,Sketch303,Pocket142,Sketch304,Pocket143,Sketch305,Pocket144,Sketch306,Pad175,+3 more]
  Origin = -> Origin026
  Placement = pos=(77,-10,0) rot=(0,0,1;4.71239rad)
  Tip = -> Pad220
COMPONENT P14 — recipe-attached ("Scoop_Rod", modeled in this document).
Construction recipe (the document's own serialized feature program — sketch geometry with constraints, then the solid features built on it; lengths are millimeters unless a unit is written):

FEATURE [Sketcher::SketchObject] Sketch354
  ArcFitTolerance = 1e-06
  AttachmentOffset = pos=(0,0,27) rot=(0,0,1;0rad)
  AttachmentSupport = -> [YZ_Plane029]
  FullyConstrained = true
  MakeInternals = false
  MapMode = 5
  Placement = pos=(27,0,0) rot=(0.57735,0.57735,0.57735;2.0944rad)
  sketch-geometry (1):
    g0: Circle CenterX=-60.15 CenterY=0 CenterZ=0 NormalX=0 NormalY=0 NormalZ=1 AngleXU=0 Radius=1.55
  constraints (3):
    c: PointOnObject(g0,g-1)
    c: Radius(g0) = 1.55
    c: DistanceX(g0,g-1) = 60.15
FEATURE [PartDesign::Pad] Pad214
  Direction = (1,0,0)
  Length = 22
  Length2 = 10
  Placement = pos=(0,0,0) rot=(1,1,1;2.0944rad)
  Profile = -> Sketch354
  ReferenceAxis = -> Sketch354 [N_Axis]
  Refine = true
  Suppressed = false
  Type = 0
FEATURE [PartDesign::Body] Body026  label="Scoop_Rod"
  AllowCompound = false
  Group = -> [Sketch354,Pad214]
  Origin = -> Origin029
  Placement = pos=(0.2,0,0) rot=(0,0,1;0rad)
  Tip = -> Pad214
COMPONENT P15 — recipe-attached ("Left_Shoulder", modeled in this document).
Construction recipe (the document's own serialized feature program — sketch geometry with constraints, then the solid features built on it; lengths are millimeters unless a unit is written):

FEATURE [Sketcher::SketchObject] Sketch075
  ArcFitTolerance = 1e-06
  AttachmentSupport = -> [XY_Plane009]
  FullyConstrained = true
  MakeInternals = false
  MapMode = 5
  sketch-geometry (7):
    g0: ArcOfCircle CenterX=0 CenterY=0 CenterZ=0 NormalX=0 NormalY=0 NormalZ=1 AngleXU=0 Radius=3 StartAngle=1.5708 EndAngle=4.71239
    g1: LineSegment StartX=-6e-16 StartY=-3 StartZ=0 EndX=4.8 EndY=-3 EndZ=0
    g2: LineSegment StartX=4.8 StartY=-3 StartZ=0 EndX=6 EndY=-1.1 EndZ=0
    g3: LineSegment StartX=6 StartY=-1.1 StartZ=0 EndX=6 EndY=4.4 EndZ=0
    g4: LineSegment StartX=6 StartY=4.4 StartZ=0 EndX=3.6 EndY=4.4 EndZ=0
    g5: LineSegment StartX=3.6 StartY=4.4 StartZ=0 EndX=3.6 EndY=3 EndZ=0
    g6: LineSegment StartX=3.6 StartY=3 StartZ=0 EndX=0 EndY=3 EndZ=0
  constraints (20):
    c: Coincident(g0,g-1)
    c: PointOnObject(g0,g-2)
    c: PointOnObject(g0,g-2)
    c: Tangent(g1,g0) = -1.5708
    c: Coincident(g2,g1)
    c: Coincident(g3,g2)
    c: Vertical(g3)
    c: Coincident(g4,g3)
    c: Horizontal(g4)
    c: Coincident(g5,g4)
    c: Vertical(g5)
    c: Coincident(g6,g5)
    c: Coincident(g6,g0)
    c: Horizontal(g6)
    c: Diameter(g0) = 6
    c: DistanceX(g0,g2) = 6
    c: DistanceX(g4,g4) = 2.4
    c: DistanceY(g3,g3) = 5.5
    c: DistanceY(g5,g5) = 1.4
    c: DistanceX(g1,g2) = 1.2
FEATURE [PartDesign::Pad] Pad039
  Direction = (0,0,1)
  Length = 8.1
  Length2 = 10
  Profile = -> Sketch075
  ReferenceAxis = -> Sketch075 [N_Axis]
  Refine = true
  Suppressed = false
  Type = 0
FEATURE [PartDesign::Plane] DatumPlane008
  AttachmentSupport = -> [Pad039]
  Length = 60
  MapMode = 5
  Placement = pos=(0,0,8.1) rot=(0,0,1;0rad)
  ResizeMode = 0
  Width = 60
FEATURE [Sketcher::SketchObject] Sketch076
  ArcFitTolerance = 1e-06
  AttachmentSupport = -> [DatumPlane008]
  FullyConstrained = true
  MakeInternals = false
  MapMode = 5
  Placement = pos=(0,0,8.1) rot=(0,0,1;0rad)
  sketch-geometry (1):
    g0: Circle CenterX=0 CenterY=0 CenterZ=0 NormalX=0 NormalY=0 NormalZ=1 AngleXU=0 Radius=1.3
  constraints (2):
    c: Coincident(g0,g-1)
    c: Diameter(g0) = 2.6
FEATURE [PartDesign::Pocket] Pocket042
  BaseFeature = -> Pad039
  Direction = (0,0,-1)
  Length = 8.1
  Length2 = 5
  Profile = -> Sketch076
  ReferenceAxis = -> Sketch076 [N_Axis]
  Refine = true
  Suppressed = false
  Type = 0
FEATURE [PartDesign::Plane] DatumPlane009
  AttachmentSupport = -> [Pocket042]
  Length = 60
  MapMode = 5
  Placement = pos=(0,4.4,0) rot=(0,0.707107,0.707107;3.14159rad)
  ResizeMode = 0
  Width = 60
FEATURE [Sketcher::SketchObject] Sketch077
  ArcFitTolerance = 1e-06
  AttachmentSupport = -> [DatumPlane009]
  ExternalGeometry = -> [Pocket042]
  FullyConstrained = true
  MakeInternals = false
  MapMode = 5
  Placement = pos=(0,4.4,0) rot=(0,0.707107,0.707107;3.14159rad)
  sketch-geometry (6):
    g0: LineSegment StartX=-4.8 StartY=0 StartZ=0 EndX=-6 EndY=1.2 EndZ=0
    g1: LineSegment StartX=-4.8 StartY=0 StartZ=0 EndX=-6 EndY=0 EndZ=0
    g2: LineSegment StartX=-6 StartY=0 StartZ=0 EndX=-6 EndY=1.2 EndZ=0
    g3: LineSegment StartX=-4.8 StartY=8.1 StartZ=0 EndX=-6 EndY=6.9 EndZ=0
    g4: LineSegment StartX=-6 StartY=6.9 StartZ=0 EndX=-6 EndY=8.1 EndZ=0
    g5: LineSegment StartX=-6 StartY=8.1 StartZ=0 EndX=-4.8 EndY=8.1 EndZ=0
  constraints (14):
    c: Symmetric(g-4,g-4,g0)
    c: PointOnObject(g0,g-5)
    c: Coincident(g1,g0)
    c: Coincident(g1,g-5)
    c: Coincident(g2,g1)
    c: Coincident(g2,g0)
    c: Symmetric(g-3,g-3,g3)
    c: PointOnObject(g3,g-5)
    c: Coincident(g4,g3)
    c: Coincident(g4,g-5)
    c: Coincident(g5,g-5)
    c: Coincident(g5,g3)
    c: Angle(g5,g3) = 0.785398
    c: Angle(g0,g1) = 0.785398
FEATURE [PartDesign::Pocket] Pocket043
  BaseFeature = -> Pocket042
  Direction = (0,-1,2e-16)
  Length = 8
  Length2 = 5
  Profile = -> Sketch077
  ReferenceAxis = -> Sketch077 [N_Axis]
  Refine = true
  Suppressed = false
  Type = 0
FEATURE [PartDesign::Plane] DatumPlane010
  AttachmentSupport = -> [Pocket043]
  Length = 60
  MapMode = 5
  Placement = pos=(6,0,0) rot=(0.57735,0.57735,0.57735;2.0944rad)
  ResizeMode = 0
  Width = 60
FEATURE [Sketcher::SketchObject] Sketch078
  ArcFitTolerance = 1e-06
  AttachmentSupport = -> [DatumPlane010]
  ExternalGeometry = -> [Pocket043]
  FullyConstrained = true
  MakeInternals = false
  MapMode = 5
  Placement = pos=(6,0,0) rot=(0.57735,0.57735,0.57735;2.0944rad)
  sketch-geometry (1):
    g0: Circle CenterX=1.65 CenterY=4.05 CenterZ=0 NormalX=0 NormalY=0 NormalZ=1 AngleXU=0 Radius=1.5
  constraints (3):
    c: Diameter(g0) = 3
    c: DistanceX(g-3,g0) = 2.75
    c: DistanceY(g0,g-3) = 2.85
FEATURE [PartDesign::Pad] Pad040
  BaseFeature = -> Pocket043
  Direction = (1,0,0)
  Length = 1.8
  Length2 = 10
  Profile = -> Sketch078
  ReferenceAxis = -> Sketch078 [N_Axis]
  Refine = true
  Suppressed = false
  Type = 0
FEATURE [PartDesign::Plane] DatumPlane011
  AttachmentSupport = -> [Pad040]
  Length = 60
  MapMode = 5
  Placement = pos=(7.8,0,0) rot=(0.57735,0.57735,0.57735;2.0944rad)
  ResizeMode = 0
  Width = 60
FEATURE [Sketcher::SketchObject] Sketch079
  ArcFitTolerance = 1e-06
  AttachmentSupport = -> [DatumPlane011]
  ExternalGeometry = -> [Pad040]
  FullyConstrained = true
  MakeInternals = false
  MapMode = 5
  Placement = pos=(7.8,0,0) rot=(0.57735,0.57735,0.57735;2.0944rad)
  sketch-geometry (1):
    g0: Circle CenterX=1.65 CenterY=4.05 CenterZ=0 NormalX=0 NormalY=0 NormalZ=1 AngleXU=0 Radius=2.5
  constraints (2):
    c: Coincident(g0,g-3)
    c: Diameter(g0) = 5
FEATURE [PartDesign::Pad] Pad041
  BaseFeature = -> Pad040
  Direction = (1,0,0)
  Length = 1.4
  Length2 = 10
  Profile = -> Sketch079
  ReferenceAxis = -> Sketch079 [N_Axis]
  Refine = true
  Suppressed = false
  Type = 0
FEATURE [PartDesign::Fillet] Fillet024
  Base = -> Pad041 [Edge7,Edge15,Edge19,Edge4,Edge3,Edge6,Edge11,Edge9,Edge10]
  BaseFeature = -> Pad041
  Radius = 0.5
  Refine = true
  SupportTransform = false
  Suppressed = false
  UseAllEdges = false
FEATURE [PartDesign::Body] Body008  label="Right_Shoulder"
  AllowCompound = false
  Group = -> [Sketch075,Pad039,DatumPlane008,Sketch076,Pocket042,DatumPlane009,Sketch077,Pocket043,DatumPlane010,Sketch078,Pad040,DatumPlane011,Sketch079,Pad041,Fillet024]
  Origin = -> Origin009
  Placement = pos=(31.15,-15,3.2) rot=(0,0,1;4.71239rad)
  Tip = -> Fillet024
COMPONENT P16 — recipe-attached ("Left_Bicept", modeled in this document).
Construction recipe (the document's own serialized feature program — sketch geometry with constraints, then the solid features built on it; lengths are millimeters unless a unit is written):

FEATURE [Sketcher::SketchObject] Sketch067
  ArcFitTolerance = 1e-06
  AttachmentSupport = -> [XY_Plane008]
  FullyConstrained = true
  MakeInternals = false
  MapMode = 5
  sketch-geometry (4):
    g0: LineSegment StartX=0 StartY=4 StartZ=0 EndX=-9.5 EndY=4 EndZ=0
    g1: LineSegment StartX=-9.5 StartY=4 StartZ=0 EndX=-9.5 EndY=-4 EndZ=0
    g2: LineSegment StartX=-9.5 StartY=-4 StartZ=0 EndX=0 EndY=-4 EndZ=0
    g3: LineSegment StartX=0 StartY=-4 StartZ=0 EndX=0 EndY=4 EndZ=0
  constraints (12):
    c: Coincident(g0,g1)
    c: Coincident(g1,g2)
    c: Coincident(g2,g3)
    c: Coincident(g3,g0)
    c: Horizontal(g0)
    c: Horizontal(g2)
    c: Vertical(g1)
    c: Vertical(g3)
    c: PointOnObject(g0,g-2)
    c: DistanceY(g3,g3) = 8
    c: DistanceY(g-1,g0) = 4
    c: DistanceX(g0,g0) = 9.5
FEATURE [PartDesign::Pad] Pad034
  Direction = (0,0,1)
  Length = 4
  Length2 = 10
  Profile = -> Sketch067
  ReferenceAxis = -> Sketch067 [N_Axis]
  Refine = true
  Suppressed = false
  Type = 0
FEATURE [PartDesign::Fillet] Fillet019
  Base = -> Pad034 [Edge1,Edge8]
  BaseFeature = -> Pad034
  Radius = 1
  Refine = true
  SupportTransform = false
  Suppressed = false
  UseAllEdges = false
FEATURE [Sketcher::SketchObject] Sketch068
  ArcFitTolerance = 1e-06
  AttachmentSupport = -> [Fillet019]
  FullyConstrained = true
  MakeInternals = false
  MapMode = 5
  Placement = pos=(0,0,4) rot=(0,0,1;0rad)
  sketch-geometry (1):
    g0: Circle CenterX=-3.15 CenterY=0 CenterZ=0 NormalX=0 NormalY=0 NormalZ=1 AngleXU=0 Radius=2.2
  constraints (3):
    c: PointOnObject(g0,g-1)
    c: Diameter(g0) = 4.4
    c: DistanceX(g0,g-1) = 3.15
FEATURE [PartDesign::Pocket] Pocket033
  BaseFeature = -> Fillet019
  Direction = (0,0,-1)
  Length = 1.6
  Length2 = 5
  Profile = -> Sketch068
  ReferenceAxis = -> Sketch068 [N_Axis]
  Refine = true
  Suppressed = false
  Type = 0
FEATURE [Sketcher::SketchObject] Sketch069
  ArcFitTolerance = 1e-06
  AttachmentSupport = -> [Pocket033]
  ExternalGeometry = -> [Pocket033]
  FullyConstrained = true
  MakeInternals = false
  MapMode = 5
  Placement = pos=(0,0,2.4) rot=(0,0,1;0rad)
  sketch-geometry (1):
    g0: Circle CenterX=-3.15 CenterY=0 CenterZ=0 NormalX=0 NormalY=0 NormalZ=1 AngleXU=0 Radius=1
  constraints (2):
    c: Coincident(g0,g-3)
    c: Diameter(g0) = 2
FEATURE [PartDesign::Pocket] Pocket034
  BaseFeature = -> Pocket033
  Direction = (0,0,-1)
  Length = 3
  Length2 = 5
  Profile = -> Sketch069
  ReferenceAxis = -> Sketch069 [N_Axis]
  Refine = true
  Suppressed = false
  Type = 0
FEATURE [PartDesign::Plane] DatumPlane004
  AttachmentSupport = -> [Pocket034]
  Length = 60
  MapMode = 5
  Placement = pos=(0,0,0) rot=(1,0,0;3.14159rad)
  ResizeMode = 0
  Width = 60
FEATURE [Sketcher::SketchObject] Sketch071
  ArcFitTolerance = 1e-06
  AttachmentSupport = -> [DatumPlane004]
  ExternalGeometry = -> [Pocket034]
  FullyConstrained = false
  MakeInternals = false
  MapMode = 5
  Placement = pos=(0,0,0) rot=(1,0,0;3.14159rad)
  sketch-geometry (4):
    g0: LineSegment StartX=-8.2 StartY=2.5 StartZ=0 EndX=-3.19862 EndY=2.5 EndZ=0
    g1: ArcOfCircle CenterX=-3.19862 CenterY=0 CenterZ=0 NormalX=0 NormalY=0 NormalZ=1 AngleXU=0 Radius=2.5 StartAngle=4.71239 EndAngle=7.85398
    g2: LineSegment StartX=-3.19862 StartY=-2.5 StartZ=0 EndX=-8.2 EndY=-2.5 EndZ=0
    g3: LineSegment StartX=-8.2 StartY=-2.5 StartZ=0 EndX=-8.2 EndY=2.5 EndZ=0
  constraints (11):
    c: Horizontal(g0)
    c: PointOnObject(g1,g-1)
    c: Coincident(g1,g0)
    c: Coincident(g2,g1)
    c: Horizontal(g2)
    c: Coincident(g3,g2)
    c: Coincident(g3,g0)
    c: Vertical(g3)
    c: Angle(g1) = 3.14159
    c: DistanceX(g-3,g2) = 1.3
    c: DistanceY(g-3,g2) = 1.5
FEATURE [PartDesign::Pocket] Pocket038
  BaseFeature = -> Pocket034
  Direction = (0,0,1)
  Length = 1
  Length2 = 5
  Profile = -> Sketch071
  ReferenceAxis = -> Sketch071 [N_Axis]
  Refine = true
  Suppressed = false
  Type = 0
FEATURE [PartDesign::Plane] DatumPlane005
  AttachmentSupport = -> [Pocket038]
  Length = 60
  MapMode = 5
  Placement = pos=(0,0,1) rot=(1,0,0;3.14159rad)
  ResizeMode = 0
  Width = 60
FEATURE [Sketcher::SketchObject] Sketch072
  ArcFitTolerance = 1e-06
  AttachmentSupport = -> [DatumPlane005]
  ExternalGeometry = -> [Pocket038]
  FullyConstrained = true
  MakeInternals = false
  MapMode = 5
  Placement = pos=(0,0,1) rot=(1,0,0;3.14159rad)
  sketch-geometry (4):
    g0: LineSegment StartX=-8.2 StartY=2.5 StartZ=0 EndX=-8.2 EndY=-2.5 EndZ=0
    g1: LineSegment StartX=-8.2 StartY=-2.5 StartZ=0 EndX=-6 EndY=-2.5 EndZ=0
    g2: LineSegment StartX=-6 StartY=-2.5 StartZ=0 EndX=-6 EndY=2.5 EndZ=0
    g3: LineSegment StartX=-6 StartY=2.5 StartZ=0 EndX=-8.2 EndY=2.5 EndZ=0
  constraints (11):
    c: Coincident(g0,g1)
    c: Coincident(g1,g2)
    c: Coincident(g2,g3)
    c: Coincident(g3,g0)
    c: Vertical(g0)
    c: Vertical(g2)
    c: Horizontal(g1)
    c: Horizontal(g3)
    c: Coincident(g0,g-4)
    c: PointOnObject(g1,g-5)
    c: DistanceX(g3,g3) = 2.2
FEATURE [PartDesign::Pocket] Pocket039
  BaseFeature = -> Pocket038
  Direction = (0,0,1)
  Length = 1.5
  Length2 = 5
  Profile = -> Sketch072
  ReferenceAxis = -> Sketch072 [N_Axis]
  Refine = true
  Suppressed = false
  Type = 0
FEATURE [PartDesign::Plane] DatumPlane007
  AttachmentSupport = -> [Pocket039]
  Length = 60
  MapMode = 5
  Placement = pos=(-9.5,0,0) rot=(0.57735,-0.57735,-0.57735;2.0944rad)
  ResizeMode = 0
  Width = 60
FEATURE [Sketcher::SketchObject] Sketch074
  ArcFitTolerance = 1e-06
  AttachmentSupport = -> [DatumPlane007]
  FullyConstrained = true
  MakeInternals = false
  MapMode = 5
  Placement = pos=(-9.5,0,0) rot=(0.57735,-0.57735,-0.57735;2.0944rad)
  sketch-geometry (1):
    g0: Circle CenterX=0 CenterY=0 CenterZ=0 NormalX=0 NormalY=0 NormalZ=1 AngleXU=0 Radius=1.5
  constraints (2):
    c: Coincident(g0,g-1)
    c: Diameter(g0) = 3
FEATURE [PartDesign::Pocket] Pocket041
  BaseFeature = -> Pocket039
  Direction = (1,0,0)
  Length = 1.3
  Length2 = 5
  Profile = -> Sketch074
  ReferenceAxis = -> Sketch074 [N_Axis]
  Refine = true
  Suppressed = false
  Type = 0
FEATURE [PartDesign::Fillet] Fillet023
  Base = -> Pocket041 [Edge24,Edge25,Edge23,Edge19,Edge4]
  BaseFeature = -> Pocket041
  Radius = 0.5
  Refine = true
  SupportTransform = false
  Suppressed = false
  UseAllEdges = false
FEATURE [PartDesign::Pad] Pad195
  BaseFeature = -> Fillet023
  Direction = (1,0,0)
  Length = 0.4
  Length2 = 10
  Profile = -> Fillet023 [Face12]
  Refine = true
  Suppressed = false
  Type = 0
FEATURE [PartDesign::Pad] Pad196
  BaseFeature = -> Pad195
  Direction = (-1,0,0)
  Length = 0.25
  Length2 = 10
  Profile = -> Pad195 [Face6]
  Refine = true
  Suppressed = false
  Type = 0
FEATURE [PartDesign::Body] Body007  label="Right_Bicept"
  AllowCompound = false
  Group = -> [Sketch067,Pad034,Fillet019,Sketch068,Pocket033,Sketch069,Pocket034,DatumPlane004,Sketch071,Pocket038,DatumPlane005,Sketch072,Pocket039,DatumPlane007,Sketch074,Pocket041,Fillet023,Pad195,Pad196]
  Origin = -> Origin008
  Placement = pos=(32.8,-30.5,7.25) rot=(0.58,-0.58,0.58;4.18879rad)
  Tip = -> Pad196
COMPONENT P17 — recipe-attached ("Left_Tricept", modeled in this document).
Construction recipe (the document's own serialized feature program — sketch geometry with constraints, then the solid features built on it; lengths are millimeters unless a unit is written):

FEATURE [Sketcher::SketchObject] Sketch060
  ArcFitTolerance = 1e-06
  AttachmentOffset = pos=(-1,0,-1.2) rot=(0,0,1;0rad)
  AttachmentSupport = -> [XY_Plane007]
  FullyConstrained = true
  MakeInternals = false
  MapMode = 5
  Placement = pos=(-1,0,-1.2) rot=(0,0,1;0rad)
  sketch-geometry (8):
    g0: ArcOfCircle CenterX=0 CenterY=0 CenterZ=0 NormalX=0 NormalY=0 NormalZ=1 AngleXU=0 Radius=3 StartAngle=4.71239 EndAngle=7.85398
    g1: LineSegment StartX=9e-16 StartY=3 StartZ=0 EndX=-3.2 EndY=3 EndZ=0
    g2: LineSegment StartX=-3.2 StartY=3 StartZ=0 EndX=-3.2 EndY=4 EndZ=0
    g3: LineSegment StartX=-3.2 StartY=4 StartZ=0 EndX=-12.7 EndY=4 EndZ=0
    g4: LineSegment StartX=-6e-16 StartY=-3 StartZ=0 EndX=-3.2 EndY=-3 EndZ=0
    g5: LineSegment StartX=-3.2 StartY=-3 StartZ=0 EndX=-3.2 EndY=-4 EndZ=0
    g6: LineSegment StartX=-3.2 StartY=-4 StartZ=0 EndX=-12.7 EndY=-4 EndZ=0
    g7: LineSegment StartX=-12.7 StartY=-4 StartZ=0 EndX=-12.7 EndY=4 EndZ=0
  constraints (23):
    c: Coincident(g0,g-1)
    c: PointOnObject(g0,g-2)
    c: PointOnObject(g0,g-2)
    c: Tangent(g1,g0) = -1.5708
    c: Coincident(g2,g1)
    c: Vertical(g2)
    c: Coincident(g3,g2)
    c: Horizontal(g3)
    c: Coincident(g4,g0)
    c: Horizontal(g4)
    c: Coincident(g5,g4)
    c: Vertical(g5)
    c: Coincident(g6,g5)
    c: Horizontal(g6)
    c: Coincident(g7,g6)
    c: Coincident(g7,g3)
    c: Vertical(g7)
    c: Diameter(g0) = 6
    c: DistanceY(g2,g2) = 1
    c: DistanceY(g5,g5) = 1
    c: DistanceX(g1,g1) = 3.2
    c: DistanceX(g4,g4) = 3.2
    c: DistanceX(g3,g3) = 9.5
FEATURE [PartDesign::Pad] Pad031
  Direction = (0,0,1)
  Length = 3.75
  Length2 = 10
  Profile = -> Sketch060
  ReferenceAxis = -> Sketch060 [N_Axis]
  Refine = true
  Suppressed = false
  Type = 0
FEATURE [Sketcher::SketchObject] Sketch061
  ArcFitTolerance = 1e-06
  AttachmentSupport = -> [Pad031]
  ExternalGeometry = -> [Pad031]
  FullyConstrained = true
  MakeInternals = false
  MapMode = 5
  Placement = pos=(0,0,2.55) rot=(0,0,1;0rad)
  sketch-geometry (1):
    g0: Circle CenterX=-1 CenterY=0 CenterZ=0 NormalX=0 NormalY=0 NormalZ=1 AngleXU=0 Radius=1.5
  constraints (3):
    c: PointOnObject(g0,g-1)
    c: Diameter(g0) = 3
    c: DistanceX(g0,g-3) = 0
FEATURE [PartDesign::Pocket] Pocket029
  BaseFeature = -> Pad031
  Direction = (0,0,-1)
  Length = 3.75
  Length2 = 5
  Profile = -> Sketch061
  ReferenceAxis = -> Sketch061 [N_Axis]
  Refine = true
  Suppressed = false
  Type = 0
FEATURE [PartDesign::Plane] DatumPlane
  AttachmentSupport = -> [Pocket029]
  Length = 60
  MapMode = 5
  Placement = pos=(0,0,2.55) rot=(0,0,1;0rad)
  ResizeMode = 0
  Width = 60
FEATURE [Sketcher::SketchObject] Sketch062
  ArcFitTolerance = 1e-06
  AttachmentSupport = -> [DatumPlane]
  FullyConstrained = true
  MakeInternals = false
  MapMode = 5
  Placement = pos=(0,0,2.55) rot=(0,0,1;0rad)
  sketch-geometry (8):
    g0: ArcOfCircle CenterX=-1 CenterY=0 CenterZ=0 NormalX=0 NormalY=0 NormalZ=1 AngleXU=0 Radius=2 StartAngle=4.71239 EndAngle=7.85398
    g1: LineSegment StartX=-12.4 StartY=-2.5 StartZ=0 EndX=-12.4 EndY=2.5 EndZ=0
    g2: LineSegment StartX=-1 StartY=2 StartZ=0 EndX=-10.2 EndY=2 EndZ=0
    g3: LineSegment StartX=-10.2 StartY=2 StartZ=0 EndX=-10.2 EndY=2.5 EndZ=0
    g4: LineSegment StartX=-10.2 StartY=2.5 StartZ=0 EndX=-12.4 EndY=2.5 EndZ=0
    g5: LineSegment StartX=-1 StartY=-2 StartZ=0 EndX=-10.2 EndY=-2 EndZ=0
    g6: LineSegment StartX=-10.2 StartY=-2 StartZ=0 EndX=-10.2 EndY=-2.5 EndZ=0
    g7: LineSegment StartX=-10.2 StartY=-2.5 StartZ=0 EndX=-12.4 EndY=-2.5 EndZ=0
  constraints (23):
    c: Coincident(g0,g-3)
    c: Vertical(g1)
    c: Diameter(g0) = 4
    c: DistanceX(g-4,g1) = 1.3
    c: DistanceY(g0,g0) = 4
    c: Tangent(g2,g0) = -1.5708
    c: Horizontal(g2)
    c: Coincident(g3,g2)
    c: Vertical(g3)
    c: Horizontal(g4)
    c: Coincident(g5,g0)
    c: Horizontal(g5)
    c: Coincident(g6,g5)
    c: Vertical(g6)
    c: Coincident(g7,g6)
    c: Horizontal(g7)
    c: DistanceY(g3,g3) = 0.5
    c: DistanceY(g6,g6) = 0.5
    c: DistanceX(g4,g4) = 2.2
    c: DistanceX(g7,g7) = 2.2
    c: Coincident(g3,g4)
    c: Coincident(g1,g4)
    c: Coincident(g1,g7)
FEATURE [PartDesign::Pocket] Pocket035
  BaseFeature = -> Pocket029
  Direction = (0,0,-1)
  Length = 2
  Length2 = 5
  Profile = -> Sketch062
  ReferenceAxis = -> Sketch062 [N_Axis]
  Refine = true
  Suppressed = false
  Type = 0
FEATURE [PartDesign::Plane] DatumPlane001
  AttachmentSupport = -> [Pocket035]
  Length = 60
  MapMode = 5
  Placement = pos=(-13.7,0,0) rot=(0.57735,-0.57735,-0.57735;2.0944rad)
  ResizeMode = 0
  Width = 60
FEATURE [Sketcher::SketchObject] Sketch063
  ArcFitTolerance = 1e-06
  AttachmentSupport = -> [DatumPlane001]
  FullyConstrained = false
  MakeInternals = false
  MapMode = 5
  Placement = pos=(-13.7,0,0) rot=(0.57735,-0.57735,-0.57735;2.0944rad)
  sketch-geometry (1):
    g0: Circle CenterX=0 CenterY=2.51194 CenterZ=0 NormalX=0 NormalY=0 NormalZ=1 AngleXU=0 Radius=1.5
  constraints (2):
    c: PointOnObject(g0,g-2)
    c: Diameter(g0) = 3
FEATURE [PartDesign::Pocket] Pocket036
  BaseFeature = -> Pocket035
  Direction = (1,0,0)
  Length = 1.3
  Length2 = 5
  Profile = -> Sketch063
  ReferenceAxis = -> Sketch063 [N_Axis]
  Refine = true
  Suppressed = false
  Type = 0
FEATURE [PartDesign::Plane] DatumPlane002
  AttachmentSupport = -> [Pocket036]
  Length = 60
  MapMode = 5
  Placement = pos=(0,0,0.55) rot=(0,0,1;0rad)
  ResizeMode = 0
  Width = 60
FEATURE [Sketcher::SketchObject] Sketch064
  ArcFitTolerance = 1e-06
  AttachmentSupport = -> [DatumPlane002]
  FullyConstrained = true
  MakeInternals = false
  MapMode = 5
  Placement = pos=(0,0,0.55) rot=(0,0,1;0rad)
  sketch-geometry (1):
    g0: Circle CenterX=-7.35 CenterY=0 CenterZ=0 NormalX=0 NormalY=0 NormalZ=1 AngleXU=0 Radius=2.2
  constraints (3):
    c: PointOnObject(g0,g-1)
    c: Diameter(g0) = 4.4
    c: DistanceX(g-3,g0) = 6.35
FEATURE [Sketcher::SketchObject] Sketch065
  ArcFitTolerance = 1e-06
  AttachmentSupport = -> [DatumPlane002]
  FullyConstrained = true
  MakeInternals = false
  MapMode = 5
  Placement = pos=(0,0,0.55) rot=(0,0,1;0rad)
  sketch-geometry (4):
    g0: LineSegment StartX=-10.2 StartY=2 StartZ=0 EndX=-10.2 EndY=-2 EndZ=0
    g1: LineSegment StartX=-10.2 StartY=-2 StartZ=0 EndX=-7.4 EndY=-2 EndZ=0
    g2: LineSegment StartX=-7.4 StartY=-2 StartZ=0 EndX=-7.4 EndY=2 EndZ=0
    g3: LineSegment StartX=-7.4 StartY=2 StartZ=0 EndX=-10.2 EndY=2 EndZ=0
  constraints (12):
    c: Coincident(g0,g1)
    c: Coincident(g1,g2)
    c: Coincident(g2,g3)
    c: Coincident(g3,g0)
    c: Vertical(g0)
    c: Vertical(g2)
    c: Horizontal(g1)
    c: Horizontal(g3)
    c: DistanceX(g-3,g0) = 2.2
    c: PointOnObject(g0,g-3)
    c: PointOnObject(g0,g-5)
    c: DistanceX(g3,g3) = 2.8
FEATURE [PartDesign::Pad] Pad037
  BaseFeature = -> Pocket036
  Direction = (0,0,1)
  Length = 3
  Length2 = 10
  Profile = -> Sketch064
  ReferenceAxis = -> Sketch064 [N_Axis]
  Refine = true
  Suppressed = false
  Type = 0
FEATURE [PartDesign::Pad] Pad038
  BaseFeature = -> Pad037
  Direction = (0,0,1)
  Length = 2
  Length2 = 10
  Profile = -> Sketch065
  ReferenceAxis = -> Sketch065 [N_Axis]
  Refine = true
  Suppressed = false
  Type = 0
FEATURE [PartDesign::Plane] DatumPlane003
  AttachmentSupport = -> [Pad038]
  Length = 60
  MapMode = 5
  Placement = pos=(0,0,3.55) rot=(0,0,1;0rad)
  ResizeMode = 0
  Width = 60
FEATURE [Sketcher::SketchObject] Sketch066
  ArcFitTolerance = 1e-06
  AttachmentSupport = -> [DatumPlane003]
  FullyConstrained = true
  MakeInternals = false
  MapMode = 5
  Placement = pos=(0,0,3.55) rot=(0,0,1;0rad)
  sketch-geometry (1):
    g0: Circle CenterX=-7.35 CenterY=0 CenterZ=0 NormalX=0 NormalY=0 NormalZ=1 AngleXU=0 Radius=0.75
  constraints (2):
    c: Coincident(g0,g-3)
    c: Diameter(g0) = 1.5
FEATURE [PartDesign::Pocket] Pocket037
  BaseFeature = -> Pad038
  Direction = (0,0,-1)
  Length = 3
  Length2 = 5
  Profile = -> Sketch066
  ReferenceAxis = -> Sketch066 [N_Axis]
  Refine = true
  Suppressed = false
  Type = 0
FEATURE [PartDesign::Fillet] Fillet022
  Base = -> Pocket037 [Edge47,Edge65]
  BaseFeature = -> Pocket037
  Radius = 0.99
  Refine = true
  SupportTransform = false
  Suppressed = false
  UseAllEdges = false
FEATURE [PartDesign::Plane] DatumPlane006
  AttachmentSupport = -> [Fillet022]
  Length = 60
  MapMode = 5
  Placement = pos=(0,0,0.55) rot=(0,0,1;0rad)
  ResizeMode = 0
  Width = 60
FEATURE [Sketcher::SketchObject] Sketch073
  ArcFitTolerance = 1e-06
  AttachmentSupport = -> [DatumPlane006]
  ExternalGeometry = -> [Fillet022]
  FullyConstrained = true
  MakeInternals = false
  MapMode = 5
  Placement = pos=(0,0,0.55) rot=(0,0,1;0rad)
  sketch-geometry (4):
    g0: LineSegment StartX=-12.4 StartY=2.5 StartZ=0 EndX=-12.4 EndY=-2.5 EndZ=0
    g1: LineSegment StartX=-12.4 StartY=-2.5 StartZ=0 EndX=-10.2 EndY=-2.5 EndZ=0
    g2: LineSegment StartX=-10.2 StartY=-2.5 StartZ=0 EndX=-10.2 EndY=2.5 EndZ=0
    g3: LineSegment StartX=-10.2 StartY=2.5 StartZ=0 EndX=-12.4 EndY=2.5 EndZ=0
  constraints (10):
    c: Coincident(g0,g1)
    c: Coincident(g1,g2)
    c: Coincident(g2,g3)
    c: Coincident(g3,g0)
    c: Vertical(g0)
    c: Vertical(g2)
    c: Horizontal(g1)
    c: Horizontal(g3)
    c: Coincident(g0,g-3)
    c: Coincident(g1,g-4)
FEATURE [PartDesign::Pocket] Pocket040
  BaseFeature = -> Fillet022
  Direction = (0,0,-1)
  Length = 0.5
  Length2 = 5
  Profile = -> Sketch073
  ReferenceAxis = -> Sketch073 [N_Axis]
  Refine = true
  Suppressed = false
  Type = 0
FEATURE [PartDesign::Pad] Pad197
  BaseFeature = -> Pocket040
  Direction = (1,0,-6e-16)
  Length = 0.4
  Length2 = 10
  Profile = -> Pocket040 [Face23]
  Refine = true
  Suppressed = false
  Type = 0
FEATURE [PartDesign::Pad] Pad198
  BaseFeature = -> Pad197
  Direction = (-1,0,0)
  Length = 0.25
  Length2 = 10
  Profile = -> Pad197 [Face23]
  Refine = true
  Suppressed = false
  Type = 0
FEATURE [Sketcher::SketchObject] Sketch338
  ArcFitTolerance = 1e-06
  AttachmentSupport = -> [Pad198]
  ExternalGeometry = -> [Pad198]
  FullyConstrained = true
  MakeInternals = false
  MapMode = 5
  Placement = pos=(0,0,0.55) rot=(0,0,1;0rad)
  sketch-geometry (2):
    g0: Circle CenterX=-1 CenterY=0 CenterZ=0 NormalX=0 NormalY=0 NormalZ=1 AngleXU=0 Radius=1.5
    g1: Circle CenterX=-1 CenterY=0 CenterZ=0 NormalX=0 NormalY=0 NormalZ=1 AngleXU=0 Radius=1.55
  constraints (5):
    c: Coincident(g0,g-3)
    c: Equal(g0,g-3)
    c: Coincident(g1,g0)
    c: Radius(g0) = 1.5
    c: Radius(g1) = 1.55
FEATURE [PartDesign::Pocket] Pocket161
  BaseFeature = -> Pad198
  Direction = (0,0,-1)
  Length = 5
  Length2 = 5
  Profile = -> Sketch338
  ReferenceAxis = -> Sketch338 [N_Axis]
  Refine = true
  Suppressed = false
  Type = 0
FEATURE [Sketcher::SketchObject] Sketch339
  ArcFitTolerance = 1e-06
  AttachmentSupport = -> [Pocket161]
  ExternalGeometry = -> [Pocket161]
  FullyConstrained = true
  MakeInternals = false
  MapMode = 5
  Placement = pos=(0,0,0.55) rot=(0,0,1;0rad)
  sketch-geometry (24):
    g0: ArcOfCircle CenterX=-1 CenterY=2e-16 CenterZ=0 NormalX=0 NormalY=0 NormalZ=1 AngleXU=0 Radius=1.55 StartAngle=1.24234 EndAngle=1.89925
    g1: ArcOfCircle CenterX=-1 CenterY=-2e-16 CenterZ=0 NormalX=0 NormalY=0 NormalZ=1 AngleXU=0 Radius=1.55 StartAngle=4.38393 EndAngle=5.04084
    g2: ArcOfCircle CenterX=-1 CenterY=1e-16 CenterZ=0 NormalX=0 NormalY=0 NormalZ=1 AngleXU=0 Radius=1.55 StartAngle=2.81314 EndAngle=3.47005
    g3: ArcOfCircle CenterX=-1 CenterY=2e-16 CenterZ=0 NormalX=0 NormalY=0 NormalZ=1 AngleXU=0 Radius=1.55 StartAngle=5.95473 EndAngle=6.61164
    g4: LineSegment [constr] StartX=-0.5 StartY=1.46714 StartZ=0 EndX=-1.5 EndY=1.46714 EndZ=0
    g5: LineSegment [constr] StartX=-2.46714 StartY=0.5 StartZ=0 EndX=-2.46714 EndY=-0.5 EndZ=0
    g6: LineSegment [constr] StartX=0.46714 StartY=0.5 StartZ=0 EndX=0.46714 EndY=-0.5 EndZ=0
    g7: LineSegment [constr] StartX=-0.5 StartY=-1.46714 StartZ=0 EndX=-1.5 EndY=-1.46714 EndZ=0
    g8: ArcOfCircle CenterX=-1 CenterY=2e-16 CenterZ=0 NormalX=0 NormalY=0 NormalZ=1 AngleXU=0 Radius=2 StartAngle=1.31812 EndAngle=1.82348
    g9: ArcOfCircle CenterX=-1 CenterY=-2e-16 CenterZ=0 NormalX=0 NormalY=0 NormalZ=1 AngleXU=0 Radius=2 StartAngle=6.03051 EndAngle=6.53587
    g10: ArcOfCircle CenterX=-1 CenterY=1e-16 CenterZ=0 NormalX=0 NormalY=0 NormalZ=1 AngleXU=0 Radius=2 StartAngle=4.45971 EndAngle=4.96507
    g11: ArcOfCircle CenterX=-1 CenterY=2e-16 CenterZ=0 NormalX=0 NormalY=0 NormalZ=1 AngleXU=0 Radius=2 StartAngle=2.88891 EndAngle=3.39427
    g12: LineSegment [constr] StartX=-2.46714 StartY=0.5 StartZ=0 EndX=-2.93649 EndY=0.5 EndZ=0
    g13: LineSegment [constr] StartX=-2.46714 StartY=-0.5 StartZ=0 EndX=-2.93649 EndY=-0.5 EndZ=0
    g14: LineSegment StartX=-2.46714 StartY=0.5 StartZ=0 EndX=-2.93649 EndY=0.5 EndZ=0
    g15: LineSegment StartX=-2.46714 StartY=-0.5 StartZ=0 EndX=-2.93649 EndY=-0.5 EndZ=0
    g16: LineSegment [constr] StartX=-0.5 StartY=1.93649 StartZ=0 EndX=-0.5 EndY=1.46714 EndZ=0
    g17: LineSegment [constr] StartX=-1.5 StartY=1.93649 StartZ=0 EndX=-1.5 EndY=1.46714 EndZ=0
    g18: LineSegment StartX=-1.5 StartY=1.93649 StartZ=0 EndX=-1.5 EndY=1.46714 EndZ=0
    g19: LineSegment StartX=-0.5 StartY=1.93649 StartZ=0 EndX=-0.5 EndY=1.46714 EndZ=0
    g20: LineSegment StartX=-1.5 StartY=-1.46714 StartZ=0 EndX=-1.5 EndY=-1.93649 EndZ=0
    g21: LineSegment StartX=-0.5 StartY=-1.46714 StartZ=0 EndX=-0.5 EndY=-1.93649 EndZ=0
    g22: LineSegment StartX=0.936492 StartY=0.5 StartZ=0 EndX=0.46714 EndY=0.5 EndZ=0
    g23: LineSegment StartX=0.936492 StartY=-0.5 StartZ=0 EndX=0.46714 EndY=-0.5 EndZ=0
  constraints (67):
    c: Tangent(g0,g-3) = -1.5708
    c: PointOnObject(g0,g-3)
    c: Tangent(g1,g-3) = -1.5708
    c: PointOnObject(g1,g-3)
    c: Tangent(g2,g-3) = -1.5708
    c: PointOnObject(g2,g-3)
    c: Tangent(g3,g-3) = -1.5708
    c: PointOnObject(g3,g-3)
    c: Coincident(g4,g0)
    c: Coincident(g4,g0)
    c: Coincident(g5,g2)
    c: Coincident(g5,g2)
    c: Coincident(g6,g3)
    c: Coincident(g6,g3)
    c: Coincident(g7,g1)
    c: Coincident(g7,g1)
    c: Horizontal(g7)
    c: Horizontal(g4)
    c: Vertical(g5)
    c: Vertical(g6)
    c: DistanceY(g5,g5) = 1
    c: DistanceY(g6,g6) = 1
    c: DistanceX(g4,g4) = 1
    c: DistanceX(g7,g7) = 1
    c: Radius(g-4) = 2
    c: Radius(g-3) = 1.55
    c: Coincident(g11,g0)
    c: Coincident(g9,g1)
    c: Coincident(g2,g10)
    c: Coincident(g8,g3)
    c: Radius(g10) = 2
    c: Radius(g11) = 2
    c: Coincident(g12,g2)
    c: Coincident(g12,g11)
    c: Horizontal(g12)
    c: Coincident(g13,g2)
    c: Coincident(g13,g11)
    c: Horizontal(g13)
    c: Coincident(g14,g2)
    c: Coincident(g14,g11)
    c: PointOnObject(g15,g11)
    c: Horizontal(g15)
    c: Coincident(g15,g2)
    c: Coincident(g16,g8)
    c: Coincident(g16,g0)
    c: Coincident(g17,g8)
    c: Coincident(g17,g0)
    c: Vertical(g17)
    c: Vertical(g16)
    c: Coincident(g18,g8)
    c: Coincident(g18,g0)
    c: Coincident(g19,g8)
    c: Coincident(g19,g0)
    c: Radius(g8) = 2
    c: Coincident(g20,g1)
    c: Coincident(g20,g10)
    c: Vertical(g20)
    c: Coincident(g21,g1)
    c: Vertical(g21)
    c: Coincident(g10,g21)
    c: Tangent(g-4,g9)
    c: Coincident(g22,g9)
    c: Coincident(g22,g3)
    c: Coincident(g23,g9)
    c: Coincident(g23,g3)
    c: Horizontal(g23)
    c: Horizontal(g22)
FEATURE [PartDesign::Pad] Pad201
  BaseFeature = -> Pocket161
  Direction = (0,0,1)
  Length = 2
  Length2 = 10
  Profile = -> Sketch339
  ReferenceAxis = -> Sketch339 [N_Axis]
  Refine = true
  Suppressed = false
  Type = 0
FEATURE [Sketcher::SketchObject] Sketch340
  ArcFitTolerance = 1e-06
  AttachmentSupport = -> [Pad201]
  ExternalGeometry = -> [Pad201]
  FullyConstrained = true
  MakeInternals = false
  MapMode = 5
  Placement = pos=(0,0,2.55) rot=(0,0,1;0rad)
  sketch-geometry (16):
    g0: ArcOfCircle CenterX=-1 CenterY=5e-16 CenterZ=0 NormalX=0 NormalY=0 NormalZ=1 AngleXU=0 Radius=1.55 StartAngle=2.81314 EndAngle=3.47005
    g1: ArcOfCircle CenterX=-1 CenterY=-2e-16 CenterZ=0 NormalX=0 NormalY=0 NormalZ=1 AngleXU=0 Radius=1.55 StartAngle=4.38393 EndAngle=5.04084
    g2: ArcOfCircle CenterX=-1 CenterY=1e-16 CenterZ=0 NormalX=0 NormalY=0 NormalZ=1 AngleXU=0 Radius=1.55 StartAngle=1.24234 EndAngle=1.89925
    g3: ArcOfCircle CenterX=-1 CenterY=-3e-16 CenterZ=0 NormalX=0 NormalY=0 NormalZ=1 AngleXU=0 Radius=1.55 StartAngle=5.95473 EndAngle=6.61164
    g4: ArcOfCircle CenterX=-1 CenterY=5e-16 CenterZ=0 NormalX=0 NormalY=0 NormalZ=1 AngleXU=0 Radius=1.5 StartAngle=2.80176 EndAngle=3.48143
    g5: ArcOfCircle CenterX=-1 CenterY=-3e-16 CenterZ=0 NormalX=0 NormalY=0 NormalZ=1 AngleXU=0 Radius=1.5 StartAngle=1.23096 EndAngle=1.91063
    g6: ArcOfCircle CenterX=-1 CenterY=-2e-16 CenterZ=0 NormalX=0 NormalY=0 NormalZ=1 AngleXU=0 Radius=1.5 StartAngle=4.37255 EndAngle=5.05223
    g7: ArcOfCircle CenterX=-1 CenterY=1e-16 CenterZ=0 NormalX=0 NormalY=0 NormalZ=1 AngleXU=0 Radius=1.5 StartAngle=5.94335 EndAngle=6.62302
    g8: LineSegment StartX=-1.5 StartY=1.46714 StartZ=0 EndX=-1.5 EndY=1.41421 EndZ=0
    g9: LineSegment StartX=-0.5 StartY=1.46714 StartZ=0 EndX=-0.5 EndY=1.41421 EndZ=0
    g10: LineSegment StartX=-2.41421 StartY=-0.5 StartZ=0 EndX=-2.46714 EndY=-0.5 EndZ=0
    g11: LineSegment StartX=-2.41421 StartY=0.5 StartZ=0 EndX=-2.46714 EndY=0.5 EndZ=0
    g12: LineSegment StartX=0.46714 StartY=-0.5 StartZ=0 EndX=0.414214 EndY=-0.5 EndZ=0
    g13: LineSegment StartX=0.414214 StartY=0.5 StartZ=0 EndX=0.46714 EndY=0.5 EndZ=0
    g14: LineSegment StartX=-0.5 StartY=-1.46714 StartZ=0 EndX=-0.5 EndY=-1.41421 EndZ=0
    g15: LineSegment StartX=-1.5 StartY=-1.46714 StartZ=0 EndX=-1.5 EndY=-1.41421 EndZ=0
  constraints (41):
    c: Tangent(g0,g-3) = -1.5708
    c: Coincident(g0,g-3)
    c: Tangent(g1,g-7) = -1.5708
    c: Coincident(g1,g-7)
    c: Tangent(g2,g-4) = -1.5708
    c: Coincident(g2,g-4)
    c: Coincident(g3,g-5)
    c: Coincident(g3,g-6)
    c: PointOnObject(g-6,g3)
    c: Coincident(g4,g0)
    c: Coincident(g6,g1)
    c: Coincident(g7,g2)
    c: Coincident(g5,g3)
    c: Radius(g5) = 1.5
    c: Radius(g7) = 1.5
    c: Radius(g6) = 1.5
    c: Radius(g4) = 1.5
    c: Coincident(g8,g2)
    c: Coincident(g8,g5)
    c: Coincident(g9,g2)
    c: Coincident(g9,g5)
    c: Vertical(g9)
    c: Vertical(g8)
    c: Coincident(g10,g4)
    c: Coincident(g10,g0)
    c: Horizontal(g10)
    c: Coincident(g11,g4)
    c: Coincident(g11,g0)
    c: Horizontal(g11)
    c: Coincident(g12,g3)
    c: Coincident(g12,g7)
    c: Coincident(g13,g7)
    c: Coincident(g13,g3)
    c: Horizontal(g13)
    c: Horizontal(g12)
    c: Coincident(g14,g1)
    c: Coincident(g14,g6)
    c: Coincident(g15,g1)
    c: Coincident(g15,g6)
    c: Vertical(g15)
    c: Vertical(g14)
FEATURE [PartDesign::Pad] Pad202
  BaseFeature = -> Pad201
  Direction = (0,0,1)
  Length = 1
  Length2 = 10
  Profile = -> Sketch340
  ReferenceAxis = -> Sketch340 [N_Axis]
  Refine = true
  Reversed = true
  Suppressed = false
  Type = 0
FEATURE [PartDesign::Body] Body006  label="Right_Tricept"
  AllowCompound = false
  Group = -> [Sketch060,Pad031,Sketch061,Pocket029,Sketch062,Sketch063,Sketch064,Sketch065,Sketch066,DatumPlane,Pocket035,DatumPlane001,Pocket036,DatumPlane002,Pad037,Pad038,DatumPlane003,Pocket037,Fillet022,DatumPlane006,Sketch073,Pocket040,Pad197,Pad198,Sketch338,Pocket161,Sketch339,Pad201,Sketch340,Pad202]
  Origin = -> Origin007
  Placement = pos=(30.25,-34.7,7.25) rot=(0.58,-0.58,0.58;4.18879rad)
  Tip = -> Pad202
COMPONENT P18 — recipe-attached ("L_Fist", modeled in this document).
Construction recipe (the document's own serialized feature program — sketch geometry with constraints, then the solid features built on it; lengths are millimeters unless a unit is written):

FEATURE [Sketcher::SketchObject] Sketch040
  ArcFitTolerance = 1e-06
  AttachmentSupport = -> [XY_Plane005]
  FullyConstrained = true
  MakeInternals = false
  MapMode = 5
  sketch-geometry (10):
    g0: ArcOfCircle CenterX=0 CenterY=0 CenterZ=0 NormalX=0 NormalY=0 NormalZ=1 AngleXU=0 Radius=1.95 StartAngle=1.5708 EndAngle=4.71239
    g1: LineSegment StartX=0 StartY=-1.95 StartZ=0 EndX=4.5 EndY=-1.95 EndZ=0
    g2: LineSegment StartX=4.5 StartY=-1.95 StartZ=0 EndX=4.5 EndY=-4 EndZ=0
    g3: LineSegment StartX=4.5 StartY=-4 StartZ=0 EndX=9.1 EndY=-4 EndZ=0
    g4: LineSegment StartX=9.1 StartY=-4 StartZ=0 EndX=11.5 EndY=-1.6 EndZ=0
    g5: LineSegment StartX=11.5 StartY=-1.6 StartZ=0 EndX=11.5 EndY=1.6 EndZ=0
    g6: LineSegment StartX=11.5 StartY=1.6 StartZ=0 EndX=9.1 EndY=4 EndZ=0
    g7: LineSegment StartX=9.1 StartY=4 StartZ=0 EndX=4.5 EndY=4 EndZ=0
    g8: LineSegment StartX=4.5 StartY=4 StartZ=0 EndX=4.5 EndY=1.95 EndZ=0
    g9: LineSegment StartX=4.5 StartY=1.95 StartZ=0 EndX=0 EndY=1.95 EndZ=0
  constraints (30):
    c: PointOnObject(g0,g-2)
    c: PointOnObject(g0,g-2)
    c: Coincident(g1,g0)
    c: Horizontal(g1)
    c: Coincident(g2,g1)
    c: Vertical(g2)
    c: Coincident(g3,g2)
    c: Horizontal(g3)
    c: Coincident(g4,g3)
    c: Coincident(g5,g4)
    c: Vertical(g5)
    c: Coincident(g6,g5)
    c: Coincident(g7,g6)
    c: Horizontal(g7)
    c: Coincident(g8,g7)
    c: Vertical(g8)
    c: Coincident(g9,g8)
    c: Coincident(g9,g0)
    c: Horizontal(g9)
    c: Coincident(g-1,g0)
    c: Diameter(g0) = 3.9
    c: DistanceY(g2,g7) = 8
    c: DistanceY(g8,g7) = 2.05
    c: DistanceX(g8,g5) = 7
    c: DistanceX(g0,g8) = 4.5
    c: DistanceX(g0,g1) = 4.5
    c: DistanceY(g4,g5) = 3.2
    c: DistanceY(g0,g5) = 1.6
    c: Angle(g6,g5) = 2.35619
    c: Angle(g5,g4) = 2.35619
FEATURE [PartDesign::Pad] Pad015
  Direction = (0,0,1)
  Length = 2.25
  Length2 = 10
  Profile = -> Sketch040
  ReferenceAxis = -> Sketch040 [N_Axis]
  Refine = true
  Suppressed = false
  Type = 0
FEATURE [Sketcher::SketchObject] Sketch041
  ArcFitTolerance = 1e-06
  AttachmentSupport = -> [Pad015]
  FullyConstrained = true
  MakeInternals = false
  MapMode = 5
  Placement = pos=(0,0,2.25) rot=(0,0,1;0rad)
  sketch-geometry (1):
    g0: Circle CenterX=0 CenterY=0 CenterZ=0 NormalX=0 NormalY=0 NormalZ=1 AngleXU=0 Radius=1
  constraints (2):
    c: Coincident(g0,g-1)
    c: Diameter(g0) = 2
FEATURE [PartDesign::Pad] Pad016
  BaseFeature = -> Pad015
  Direction = (0,0,1)
  Length = 1.3
  Length2 = 10
  Profile = -> Sketch041
  ReferenceAxis = -> Sketch041 [N_Axis]
  Refine = true
  Suppressed = false
  Type = 0
FEATURE [Sketcher::SketchObject] Sketch042
  ArcFitTolerance = 1e-06
  AttachmentSupport = -> [Pad016]
  FullyConstrained = true
  MakeInternals = false
  MapMode = 5
  Placement = pos=(0,0,0) rot=(1,0,0;3.14159rad)
  sketch-geometry (1):
    g0: Circle CenterX=0 CenterY=0 CenterZ=0 NormalX=0 NormalY=0 NormalZ=1 AngleXU=0 Radius=1
  constraints (2):
    c: Coincident(g0,g-1)
    c: Diameter(g0) = 2
FEATURE [PartDesign::Pad] Pad017
  BaseFeature = -> Pad016
  Direction = (0,0,-1)
  Length = 1.3
  Length2 = 10
  Profile = -> Sketch042
  ReferenceAxis = -> Sketch042 [N_Axis]
  Refine = true
  Suppressed = false
  Type = 0
FEATURE [Sketcher::SketchObject] Sketch043
  ArcFitTolerance = 1e-06
  AttachmentSupport = -> [Pad017]
  ExternalGeometry = -> [Pad017]
  FullyConstrained = true
  MakeInternals = false
  MapMode = 5
  Placement = pos=(0,0,0) rot=(1,0,0;3.14159rad)
  sketch-geometry (6):
    g0: LineSegment StartX=4.5 StartY=4 StartZ=0 EndX=9.1 EndY=4 EndZ=0
    g1: LineSegment StartX=9.1 StartY=4 StartZ=0 EndX=11.5 EndY=1.6 EndZ=0
    g2: LineSegment StartX=11.5 StartY=1.6 StartZ=0 EndX=11.5 EndY=-1.6 EndZ=0
    g3: LineSegment StartX=11.5 StartY=-1.6 StartZ=0 EndX=9.1 EndY=-4 EndZ=0
    g4: LineSegment StartX=9.1 StartY=-4 StartZ=0 EndX=4.5 EndY=-4 EndZ=0
    g5: LineSegment StartX=4.5 StartY=-4 StartZ=0 EndX=4.5 EndY=4 EndZ=0
  constraints (12):
    c: Coincident(g0,g-3)
    c: Coincident(g0,g-4)
    c: Coincident(g1,g0)
    c: Coincident(g1,g-5)
    c: Coincident(g2,g1)
    c: Coincident(g2,g-6)
    c: Coincident(g3,g2)
    c: Coincident(g3,g-7)
    c: Coincident(g4,g3)
    c: Coincident(g4,g-7)
    c: Coincident(g5,g4)
    c: Coincident(g5,g0)
FEATURE [PartDesign::Pocket] Pocket025
  BaseFeature = -> Pad017
  Direction = (0,0,1)
  Length = 1.25
  Length2 = 5
  Profile = -> Sketch043
  ReferenceAxis = -> Sketch043 [N_Axis]
  Refine = true
  Suppressed = false
  Type = 0
FEATURE [Sketcher::SketchObject] Sketch044
  ArcFitTolerance = 1e-06
  AttachmentSupport = -> [Pocket025]
  ExternalGeometry = -> [Pocket025]
  FullyConstrained = true
  MakeInternals = false
  MapMode = 5
  Placement = pos=(0,0,2.25) rot=(0,0,1;0rad)
  sketch-geometry (6):
    g0: LineSegment StartX=4.5 StartY=4 StartZ=0 EndX=9.1 EndY=4 EndZ=0
    g1: LineSegment StartX=9.1 StartY=4 StartZ=0 EndX=11.5 EndY=1.6 EndZ=0
    g2: LineSegment StartX=11.5 StartY=1.6 StartZ=0 EndX=11.5 EndY=-1.6 EndZ=0
    g3: LineSegment StartX=11.5 StartY=-1.6 StartZ=0 EndX=9.1 EndY=-4 EndZ=0
    g4: LineSegment StartX=9.1 StartY=-4 StartZ=0 EndX=4.5 EndY=-4 EndZ=0
    g5: LineSegment StartX=4.5 StartY=-4 StartZ=0 EndX=4.5 EndY=4 EndZ=0
  constraints (12):
    c: Coincident(g0,g-3)
    c: Coincident(g0,g-4)
    c: Coincident(g1,g0)
    c: Coincident(g1,g-5)
    c: Coincident(g2,g1)
    c: Coincident(g2,g-6)
    c: Coincident(g3,g2)
    c: Coincident(g3,g-7)
    c: Coincident(g4,g3)
    c: Coincident(g4,g-7)
    c: Coincident(g5,g4)
    c: Coincident(g5,g0)
FEATURE [PartDesign::Pad] Pad018
  BaseFeature = -> Pocket025
  Direction = (0,0,1)
  Length = 1
  Length2 = 10
  Profile = -> Sketch044
  ReferenceAxis = -> Sketch044 [N_Axis]
  Refine = true
  Suppressed = false
  Type = 0
FEATURE [Sketcher::SketchObject] Sketch045
  ArcFitTolerance = 1e-06
  AttachmentSupport = -> [Pad018]
  ExternalGeometry = -> [Pad018]
  FullyConstrained = true
  MakeInternals = false
  MapMode = 5
  Placement = pos=(0,0,3.25) rot=(0,0,1;0rad)
  sketch-geometry (6):
    g0: LineSegment StartX=4.5 StartY=3.4 StartZ=0 EndX=8.85147 EndY=3.4 EndZ=0
    g1: LineSegment StartX=8.85147 StartY=3.4 StartZ=0 EndX=10.9 EndY=1.35147 EndZ=0
    g2: LineSegment StartX=10.9 StartY=1.35147 StartZ=0 EndX=10.9 EndY=-1.35147 EndZ=0
    g3: LineSegment StartX=10.9 StartY=-1.35147 StartZ=0 EndX=8.25147 EndY=-4 EndZ=0
    g4: LineSegment StartX=8.25147 StartY=-4 StartZ=0 EndX=4.5 EndY=-4 EndZ=0
    g5: LineSegment StartX=4.5 StartY=3.4 StartZ=0 EndX=4.5 EndY=-4 EndZ=0
  constraints (17):
    c: PointOnObject(g0,g-8)
    c: Horizontal(g0)
    c: Coincident(g1,g0)
    c: Coincident(g2,g1)
    c: Vertical(g2)
    c: Coincident(g3,g2)
    c: Coincident(g4,g3)
    c: Horizontal(g4)
    c: DistanceX(g1,g-5) = 0.6
    c: DistanceY(g0,g-4) = 0.6
    c: Angle(g0,g1) = 2.35619
    c: Angle(g2,g3) = 2.35619
    c: Distance(g0,g-4) = 0.6
    c: Distance(g3,g-6) = 0.6
    c: Coincident(g5,g0)
    c: Coincident(g5,g4)
    c: Coincident(g4,g-8)
FEATURE [PartDesign::Pad] Pad019
  BaseFeature = -> Pad018
  Direction = (0,0,1)
  Length = 1.7
  Length2 = 10
  Profile = -> Sketch045
  ReferenceAxis = -> Sketch045 [N_Axis]
  Refine = true
  Suppressed = false
  Type = 0
FEATURE [Sketcher::SketchObject] Sketch046
  ArcFitTolerance = 1e-06
  AttachmentSupport = -> [Pad019]
  ExternalGeometry = -> [Pad019]
  FullyConstrained = true
  MakeInternals = false
  MapMode = 5
  Placement = pos=(0,0,1.25) rot=(1,0,0;3.14159rad)
  sketch-geometry (9):
    g0: LineSegment StartX=4.5 StartY=4 StartZ=0 EndX=8.25147 EndY=4 EndZ=0
    g1: LineSegment StartX=8.25147 StartY=4 StartZ=0 EndX=10.7 EndY=1.55147 EndZ=0
    g2: LineSegment StartX=10.7 StartY=1.55147 StartZ=0 EndX=10.7 EndY=-1.55147 EndZ=0
    g3: LineSegment StartX=4.5 StartY=4 StartZ=0 EndX=4.5 EndY=-3.4 EndZ=0
    g4: LineSegment StartX=4.5 StartY=-3.4 StartZ=0 EndX=5.5 EndY=-3.4 EndZ=0
    g5: LineSegment StartX=5.5 StartY=-3.4 StartZ=0 EndX=7 EndY=-1.9 EndZ=0
    g6: LineSegment StartX=10.7 StartY=-1.55147 StartZ=0 EndX=9.45147 EndY=-2.8 EndZ=0
    g7: LineSegment StartX=9.45147 StartY=-2.8 StartZ=0 EndX=7 EndY=-2.8 EndZ=0
    g8: LineSegment StartX=7 StartY=-2.8 StartZ=0 EndX=7 EndY=-1.9 EndZ=0
  constraints (26):
    c: Horizontal(g0)
    c: Coincident(g1,g0)
    c: Coincident(g2,g1)
    c: Vertical(g2)
    c: DistanceX(g2,g-6) = 0.8
    c: Angle(g1,g2) = 2.35619
    c: Coincident(g3,g0)
    c: Vertical(g3)
    c: Coincident(g4,g3)
    c: Horizontal(g4)
    c: Coincident(g5,g4)
    c: Angle(g5,g4) = 2.35619
    c: DistanceY(g-7,g4) = 0.6
    c: DistanceX(g4,g4) = 1
    c: Distance(g2,g-6) = 0.6
    c: Coincident(g0,g-8)
    c: Distance(g1,g-4) = 0.6
    c: Coincident(g6,g2)
    c: Coincident(g7,g6)
    c: Horizontal(g7)
    c: Parallel(g6,g-6)
    c: Coincident(g8,g7)
    c: Vertical(g8)
    c: Coincident(g5,g8)
    c: DistanceX(g-9,g5) = 2.5
    c: DistanceY(g-7,g7) = 1.2
FEATURE [Sketcher::SketchObject] Sketch047
  ArcFitTolerance = 1e-06
  FullyConstrained = true
  MakeInternals = false
  MapMode = 5
  Placement = pos=(0,0,-0.65) rot=(1,0,0;3.14159rad)
  sketch-geometry (8):
    g0: LineSegment StartX=4.5 StartY=4.25 StartZ=0 EndX=7.70147 EndY=4.25 EndZ=0
    g1: LineSegment StartX=7.70147 StartY=4.25 StartZ=0 EndX=10.4 EndY=1.55147 EndZ=0
    g2: LineSegment StartX=10.4 StartY=1.55147 StartZ=0 EndX=10.4 EndY=-1.53431 EndZ=0
    g3: LineSegment StartX=10.4 StartY=-1.53431 StartZ=0 EndX=7.3 EndY=-1.53431 EndZ=0
    g4: LineSegment StartX=7.3 StartY=-1.53431 StartZ=0 EndX=7.3 EndY=-1.55 EndZ=0
    g5: LineSegment StartX=7.3 StartY=-1.55 StartZ=0 EndX=5.5 EndY=-3.35 EndZ=0
    g6: LineSegment StartX=5.5 StartY=-3.35 StartZ=0 EndX=4.5 EndY=-3.35 EndZ=0
    g7: LineSegment StartX=4.5 StartY=-3.35 StartZ=0 EndX=4.5 EndY=4.25 EndZ=0
  constraints (21):
    c: Horizontal(g0)
    c: Coincident(g1,g0)
    c: Coincident(g2,g1)
    c: Vertical(g2)
    c: Coincident(g3,g2)
    c: Horizontal(g3)
    c: Coincident(g4,g3)
    c: Vertical(g4)
    c: Coincident(g5,g4)
    c: Coincident(g6,g5)
    c: Coincident(g7,g6)
    c: Coincident(g7,g0)
    c: Coincident(g0,g-9)
    c: DistanceX(g0,g-4) = 0.3
    c: DistanceX(g1,g-5) = 0.3
    c: Angle(g0,g1) = 2.35619
    c: DistanceY(g-7,g3) = 0.3
    c: Coincident(g6,g-9)
    c: Coincident(g5,g-8)
    c: Angle(g5,g6) = 2.35619
    c: DistanceX(g-8,g3) = 0.3
FEATURE [PartDesign::Pad] Pad021
  BaseFeature = -> Pad019
  Direction = (0,0,-1)
  Length = 1.9
  Length2 = 10
  Profile = -> Sketch047
  ReferenceAxis = -> Sketch047 [N_Axis]
  Refine = true
  Suppressed = false
  Type = 0
FEATURE [Sketcher::SketchObject] Sketch048
  ArcFitTolerance = 1e-06
  AttachmentSupport = -> [Pad021]
  ExternalGeometry = -> [Pad021]
  FullyConstrained = true
  MakeInternals = false
  MapMode = 5
  Placement = pos=(0,0,4.95) rot=(0,0,1;0rad)
  sketch-geometry (1):
    g0: Circle CenterX=8.075 CenterY=0 CenterZ=0 NormalX=0 NormalY=0 NormalZ=1 AngleXU=0 Radius=1.425
  constraints (3):
    c: Diameter(g0) = 2.85
    c: DistanceX(g-4,g0) = 3.575
    c: PointOnObject(g0,g-1)
FEATURE [PartDesign::Pocket] Pocket026
  BaseFeature = -> Pad021
  Direction = (0,0,-1)
  Length = 6
  Length2 = 5
  Profile = -> Sketch048
  ReferenceAxis = -> Sketch048 [N_Axis]
  Refine = true
  Suppressed = false
  Type = 0
FEATURE [Sketcher::SketchObject] Sketch049
  ArcFitTolerance = 1e-06
  AttachmentSupport = -> [Pocket026]
  ExternalGeometry = -> [Pocket026]
  FullyConstrained = true
  MakeInternals = false
  MapMode = 5
  Placement = pos=(0,4,0) rot=(0,0.707107,0.707107;3.14159rad)
  sketch-geometry (7):
    g0: LineSegment StartX=-4.5 StartY=4.95 StartZ=0 EndX=-8.5 EndY=4.95 EndZ=0
    g1: LineSegment StartX=-8.5 StartY=4.95 StartZ=0 EndX=-9.5 EndY=3.95 EndZ=0
    g2: LineSegment StartX=-9.5 StartY=0.25 StartZ=0 EndX=-7.5 EndY=0.25 EndZ=0
    g3: LineSegment StartX=-7.5 StartY=0.25 StartZ=0 EndX=-7.5 EndY=1.25 EndZ=0
    g4: LineSegment StartX=-7.5 StartY=1.25 StartZ=0 EndX=-4.5 EndY=1.25 EndZ=0
    g5: LineSegment StartX=-4.5 StartY=1.25 StartZ=0 EndX=-4.5 EndY=4.95 EndZ=0
    g6: LineSegment StartX=-9.5 StartY=3.95 StartZ=0 EndX=-9.5 EndY=0.25 EndZ=0
  constraints (19):
    c: Angle(g1,g0) = 2.35619
    c: Coincident(g1,g0)
    c: Coincident(g6,g1)
    c: Vertical(g6)
    c: Coincident(g2,g6)
    c: Horizontal(g0)
    c: Coincident(g0,g5)
    c: Coincident(g0,g-3)
    c: Coincident(g5,g-4)
    c: Coincident(g4,g5)
    c: Horizontal(g2)
    c: Horizontal(g4)
    c: Vertical(g3)
    c: DistanceY(g3,g3) = 1
    c: DistanceX(g0,g0) = 4
    c: DistanceX(g4,g4) = 3
    c: DistanceX(g2,g2) = 2
    c: Coincident(g2,g3)
    c: Coincident(g3,g4)
FEATURE [PartDesign::Pad] Pad022
  BaseFeature = -> Pocket026
  Direction = (0,1,-2e-16)
  Length = 2.5
  Length2 = 10
  Profile = -> Sketch049
  ReferenceAxis = -> Sketch049 [N_Axis]
  Refine = true
  Reversed = true
  Suppressed = false
  Type = 0
FEATURE [PartDesign::Pad] Pad035
  BaseFeature = -> Pad022
  Direction = (0,0,-1)
  Length = 1.9
  Length2 = 10
  Profile = -> Sketch046
  ReferenceAxis = -> Sketch046 [N_Axis]
  Refine = true
  Suppressed = false
  Type = 0
FEATURE [Sketcher::SketchObject] Sketch070
  ArcFitTolerance = 1e-06
  AttachmentSupport = -> [Pad035]
  ExternalGeometry = -> [Pad035]
  FullyConstrained = true
  MakeInternals = false
  MapMode = 5
  Placement = pos=(0,0,-0.65) rot=(1,0,0;3.14159rad)
  sketch-geometry (9):
    g0: LineSegment StartX=4.5 StartY=4 StartZ=0 EndX=4.5 EndY=-3.4 EndZ=0
    g1: LineSegment StartX=4.5 StartY=-3.4 StartZ=0 EndX=5.5 EndY=-3.4 EndZ=0
    g2: LineSegment StartX=5.5 StartY=-3.4 StartZ=0 EndX=7 EndY=-1.9 EndZ=0
    g3: LineSegment StartX=7 StartY=-1.9 StartZ=0 EndX=7 EndY=-2.35 EndZ=0
    g4: LineSegment StartX=7 StartY=-2.35 StartZ=0 EndX=9.23353 EndY=-2.35 EndZ=0
    g5: LineSegment StartX=9.23353 StartY=-2.35 StartZ=0 EndX=10.2178 EndY=-1.41921 EndZ=0
    g6: LineSegment StartX=7.63702 StartY=4 StartZ=0 EndX=10.2178 EndY=1.41921 EndZ=0
    g7: LineSegment StartX=10.2178 StartY=1.41921 StartZ=0 EndX=10.2178 EndY=-1.41921 EndZ=0
    g8: LineSegment StartX=7.63702 StartY=4 StartZ=0 EndX=4.5 EndY=4 EndZ=0
  constraints (22):
    c: Coincident(g0,g-4)
    c: Coincident(g0,g-11)
    c: Coincident(g1,g0)
    c: Coincident(g1,g-11)
    c: Coincident(g2,g1)
    c: Coincident(g2,g-10)
    c: Coincident(g3,g2)
    c: Symmetric(g-9,g-9,g3)
    c: Coincident(g4,g3)
    c: Horizontal(g4)
    c: Coincident(g5,g4)
    c: Coincident(g7,g6)
    c: Coincident(g7,g5)
    c: Vertical(g7)
    c: Angle(g7,g5) = 2.32827
    c: Distance(g6,g-6) = 0.5
    c: Distance(g4,g-8) = 0.5
    c: Distance(g5,g-7) = 0.5
    c: Coincident(g8,g6)
    c: Coincident(g8,g0)
    c: Horizontal(g8)
    c: Angle(g8,g6) = 2.35619
FEATURE [PartDesign::Pad] Pad036
  BaseFeature = -> Pad035
  Direction = (0,0,-1)
  Length = 1.9
  Length2 = 10
  Profile = -> Sketch070
  ReferenceAxis = -> Sketch070 [N_Axis]
  Refine = true
  Suppressed = false
  Type = 0
FEATURE [PartDesign::Fillet] Fillet021
  Base = -> Pad036 [Edge14,Edge8,Edge7,Edge88,Edge76,Edge89]
  BaseFeature = -> Pad036
  Radius = 0.5
  Refine = true
  SupportTransform = false
  Suppressed = false
  UseAllEdges = false
FEATURE [Sketcher::SketchObject] Sketch337
  ArcFitTolerance = 1e-06
  AttachmentSupport = -> [Fillet021]
  ExternalGeometry = -> [Fillet021]
  FullyConstrained = true
  MakeInternals = false
  MapMode = 5
  Placement = pos=(0,0,4.95) rot=(0,0,1;0rad)
  sketch-geometry (1):
    g0: Circle CenterX=8.075 CenterY=0 CenterZ=0 NormalX=0 NormalY=0 NormalZ=1 AngleXU=0 Radius=1.45
  constraints (2):
    c: Coincident(g0,g-3)
    c: Radius(g0) = 1.45
FEATURE [PartDesign::Pocket] Pocket160
  BaseFeature = -> Fillet021
  Direction = (0,0,-1)
  Length = 3.7
  Length2 = 5
  Profile = -> Sketch337
  ReferenceAxis = -> Sketch337 [N_Axis]
  Refine = true
  Suppressed = false
  Type = 0
FEATURE [PartDesign::Body] Body004  label="Right_Fist"
  AllowCompound = false
  Group = -> [Sketch040,Pad015,Sketch041,Pad016,Sketch042,Pad017,Sketch043,Pocket025,Sketch044,Pad018,Sketch045,Pad019,Sketch046,Sketch047,Pad021,Sketch048,Pocket026,Sketch049,Pad022,Pad035,Sketch070,Pad036,Fillet021,Sketch337,Pocket160]
  Origin = -> Origin005
  Placement = pos=(31.8,-44.2,7.25) rot=(0.58,-0.58,0.58;4.18879rad)
  Tip = -> Pocket160
COMPONENT P19 — recipe-attached ("Left_Forearm", modeled in this document).
Construction recipe (the document's own serialized feature program — sketch geometry with constraints, then the solid features built on it; lengths are millimeters unless a unit is written):

FEATURE [Sketcher::SketchObject] Sketch
  ArcFitTolerance = 1e-06
  AttachmentSupport = -> [XY_Plane]
  FullyConstrained = true
  MakeInternals = false
  MapMode = 5
  sketch-geometry (8):
    g0: LineSegment StartX=0 StartY=4 StartZ=0 EndX=-11.3 EndY=4 EndZ=0
    g1: LineSegment StartX=-11.3 StartY=4 StartZ=0 EndX=-11.6 EndY=3.15 EndZ=0
    g2: LineSegment StartX=-11.6 StartY=3.15 StartZ=0 EndX=-14.9 EndY=3.15 EndZ=0
    g3: ArcOfCircle CenterX=-14.9 CenterY=0 CenterZ=0 NormalX=0 NormalY=0 NormalZ=1 AngleXU=0 Radius=3.15 StartAngle=1.5708 EndAngle=4.71239
    g4: LineSegment StartX=-14.9 StartY=-3.15 StartZ=0 EndX=-11.6 EndY=-3.15 EndZ=0
    g5: LineSegment StartX=-11.6 StartY=-3.15 StartZ=0 EndX=-11.3 EndY=-4 EndZ=0
    g6: LineSegment StartX=-11.3 StartY=-4 StartZ=0 EndX=0 EndY=-4 EndZ=0
    g7: LineSegment StartX=0 StartY=-4 StartZ=0 EndX=0 EndY=4 EndZ=0
  constraints (25):
    c: Horizontal(g0)
    c: Coincident(g1,g0)
    c: Coincident(g2,g1)
    c: Horizontal(g2)
    c: PointOnObject(g3,g-1)
    c: Coincident(g3,g2)
    c: Coincident(g4,g3)
    c: Horizontal(g4)
    c: Coincident(g5,g4)
    c: Coincident(g6,g5)
    c: Horizontal(g6)
    c: Coincident(g7,g6)
    c: Coincident(g7,g0)
    c: Vertical(g7)
    c: DistanceY(g6,g0) = 8
    c: DistanceY(g6,g-1) = 4
    c: DistanceX(g0,g0) = 11.3
    c: DistanceX(g5,g6) = 11.3
    c: PointOnObject(g-1,g7)
    c: DistanceY(g3,g2) = 6.3
    c: DistanceX(g1,g0) = 11.6
    c: DistanceX(g4,g6) = 11.6
    c: DistanceX(g2,g0) = 14.9
    c: DistanceX(g3,g6) = 14.9
    c: Radius(g3) = 3.15
FEATURE [PartDesign::Pad] Pad
  Direction = (0,0,1)
  Length = 4.1
  Length2 = 10
  Profile = -> Sketch
  ReferenceAxis = -> Sketch [N_Axis]
  Refine = true
  Suppressed = false
  Type = 0
FEATURE [Sketcher::SketchObject] Sketch001
  ArcFitTolerance = 1e-06
  FullyConstrained = true
  MakeInternals = false
  MapMode = 5
  Placement = pos=(0,0,4.1) rot=(0,0,1;0rad)
  sketch-geometry (2):
    g0: Circle CenterX=-14.9 CenterY=0 CenterZ=0 NormalX=0 NormalY=0 NormalZ=1 AngleXU=0 Radius=1.55
    g1: Circle CenterX=-8.4 CenterY=0 CenterZ=0 NormalX=0 NormalY=0 NormalZ=1 AngleXU=0 Radius=1
  constraints (6):
    c: PointOnObject(g0,g-1)
    c: PointOnObject(g1,g-1)
    c: Diameter(g0) = 3.1
    c: Diameter(g1) = 2
    c: DistanceX(g0,g-1) = 14.9
    c: DistanceX(g1,g-1) = 8.4
FEATURE [Sketcher::SketchObject] Sketch002
  ArcFitTolerance = 1e-06
  FullyConstrained = true
  MakeInternals = false
  MapMode = 5
  Placement = pos=(0,0,4.1) rot=(0,0,1;0rad)
  sketch-geometry (1):
    g0: Circle CenterX=-8.4 CenterY=0 CenterZ=0 NormalX=0 NormalY=0 NormalZ=1 AngleXU=0 Radius=2.2
  constraints (3):
    c: PointOnObject(g0,g-1)
    c: DistanceX(g0,g-1) = 8.4
    c: Diameter(g0) = 4.4
FEATURE [PartDesign::Pocket] Pocket
  BaseFeature = -> Pad
  Direction = (0,0,-1)
  Length = 5
  Length2 = 5
  Profile = -> Sketch001
  ReferenceAxis = -> Sketch001 [N_Axis]
  Refine = true
  Suppressed = false
  Type = 0
FEATURE [PartDesign::Pocket] Pocket001
  BaseFeature = -> Pocket
  Direction = (0,0,-1)
  Length = 1.25
  Length2 = 5
  Profile = -> Sketch002
  ReferenceAxis = -> Sketch002 [N_Axis]
  Refine = true
  Suppressed = false
  Type = 0
FEATURE [Sketcher::SketchObject] Sketch003
  ArcFitTolerance = 1e-06
  AttachmentSupport = -> [Pocket001]
  FullyConstrained = true
  MakeInternals = false
  MapMode = 5
  Placement = pos=(0,0,0) rot=(1,0,0;3.14159rad)
  sketch-geometry (1):
    g0: Circle CenterX=-8.4 CenterY=0 CenterZ=0 NormalX=0 NormalY=0 NormalZ=1 AngleXU=0 Radius=2.25
  constraints (3):
    c: PointOnObject(g0,g-1)
    c: DistanceX(g0,g-1) = 8.4
    c: Diameter(g0) = 4.5
FEATURE [Sketcher::SketchObject] Sketch004
  ArcFitTolerance = 1e-06
  AttachmentSupport = -> [Pocket001]
  FullyConstrained = true
  MakeInternals = false
  MapMode = 5
  Placement = pos=(0,0,0) rot=(1,0,0;3.14159rad)
  sketch-geometry (1):
    g0: Circle CenterX=-4.4 CenterY=0 CenterZ=0 NormalX=0 NormalY=0 NormalZ=1 AngleXU=0 Radius=1.05
  constraints (3):
    c: PointOnObject(g0,g-1)
    c: Diameter(g0) = 2.1
    c: DistanceX(g0,g-1) = 4.4
FEATURE [PartDesign::Pocket] Pocket002
  BaseFeature = -> Pocket001
  Direction = (0,0,1)
  Length = 3.5
  Length2 = 5
  Profile = -> Sketch004
  ReferenceAxis = -> Sketch004 [N_Axis]
  Refine = true
  Suppressed = false
  Type = 0
FEATURE [PartDesign::Pocket] Pocket003
  BaseFeature = -> Pocket002
  Direction = (0,0,1)
  Length = 1.25
  Length2 = 5
  Profile = -> Sketch003
  ReferenceAxis = -> Sketch003 [N_Axis]
  Refine = true
  Suppressed = false
  Type = 0
FEATURE [Sketcher::SketchObject] Sketch005
  ArcFitTolerance = 1e-06
  AttachmentSupport = -> [Pocket003]
  FullyConstrained = true
  MakeInternals = false
  MapMode = 5
  Placement = pos=(0,0,0) rot=(1,0,0;3.14159rad)
  sketch-geometry (4):
    g0: LineSegment StartX=0 StartY=2 StartZ=0 EndX=-4.4 EndY=2 EndZ=0
    g1: ArcOfCircle CenterX=-4.39999 CenterY=0 CenterZ=0 NormalX=0 NormalY=0 NormalZ=1 AngleXU=0 Radius=2 StartAngle=1.5708 EndAngle=4.71238
    g2: LineSegment StartX=-4.4 StartY=-2 StartZ=0 EndX=0 EndY=-2 EndZ=0
    g3: LineSegment StartX=0 StartY=2 StartZ=0 EndX=0 EndY=-2 EndZ=0
  constraints (13):
    c: PointOnObject(g0,g-2)
    c: Horizontal(g0)
    c: PointOnObject(g1,g-1)
    c: Coincident(g1,g0)
    c: Coincident(g2,g1)
    c: PointOnObject(g2,g-2)
    c: Horizontal(g2)
    c: Coincident(g3,g0)
    c: Coincident(g3,g2)
    c: DistanceY(g2,g0) = 4
    c: DistanceX(g0,g0) = 4.4
    c: DistanceX(g1,g2) = 4.4
    c: Diameter(g1) = 4
FEATURE [PartDesign::Pocket] Pocket013
  BaseFeature = -> Pocket003
  Direction = (0,0,1)
  Length = 1.25
  Length2 = 5
  Profile = -> Sketch005
  ReferenceAxis = -> Sketch005 [N_Axis]
  Refine = true
  Suppressed = false
  Type = 0
FEATURE [PartDesign::Fillet] Fillet
  Base = -> Pocket013 [Edge4,Vertex4,Edge14,Edge2,Edge27,Edge29,Edge30,Edge28,Edge37,Edge26,Edge10,Edge11,Edge1]
  BaseFeature = -> Pocket013
  Radius = 0.5
  Refine = true
  SupportTransform = false
  Suppressed = false
  UseAllEdges = false
FEATURE [PartDesign::Body] Body  label="Right_Forearm"
  AllowCompound = false
  Group = -> [Sketch,Pad,Sketch001,Sketch002,Pocket,Pocket001,Sketch003,Sketch004,Pocket002,Pocket003,Sketch005,Pocket013,Fillet]
  Origin = -> Origin
  Placement = pos=(32.8,-48.6,7.25) rot=(0.57735,-0.57735,0.57735;4.18879rad)
  Tip = -> Fillet
COMPONENT P20 — recipe-attached ("Left_Foot", modeled in this document).
Construction recipe (the document's own serialized feature program — sketch geometry with constraints, then the solid features built on it; lengths are millimeters unless a unit is written):

FEATURE [Sketcher::SketchObject] Sketch196
  ArcFitTolerance = 1e-06
  AttachmentSupport = -> [XY_Plane018]
  FullyConstrained = false
  MakeInternals = false
  MapMode = 5
  sketch-geometry (5):
    g0: LineSegment StartX=19.17 StartY=-5.55 StartZ=0 EndX=42.05 EndY=-5.55 EndZ=0
    g1: ArcOfCircle CenterX=42.05 CenterY=0 CenterZ=0 NormalX=0 NormalY=0 NormalZ=1 AngleXU=0 Radius=5.55 StartAngle=4.71239 EndAngle=7.85398
    g2: LineSegment StartX=19.17 StartY=-5.55 StartZ=0 EndX=19.17 EndY=1.23148 EndZ=0
    g3: ArcOfCircle CenterX=24.17 CenterY=1.23148 CenterZ=0 NormalX=0 NormalY=0 NormalZ=1 AngleXU=0 Radius=5 StartAngle=2.09902 EndAngle=3.14159
    g4: LineSegment StartX=21.65 StartY=5.55 StartZ=0 EndX=42.05 EndY=5.55 EndZ=0
  constraints (16):
    c: Horizontal(g0)
    c: Coincident(g1,g0)
    c: Coincident(g2,g0)
    c: Vertical(g2)
    c: Coincident(g3,g2)
    c: Coincident(g4,g3)
    c: Coincident(g4,g1)
    c: Horizontal(g4)
    c: DistanceX(g0,g0) = 22.88
    c: Radius(g1) = 5.55
    c: PointOnObject(g1,g-1)
    c: Radius(g3) = 5
    c: DistanceY(g0,g1) = 11.1
    c: DistanceY(g2,g3) = 0
    c: DistanceX(g-1,g1) = 42.05
    c: DistanceX(g3,g3) = 2.52
FEATURE [PartDesign::Pad] Pad104
  Direction = (0,0,1)
  Length = 1.9
  Length2 = 10
  Profile = -> Sketch196
  ReferenceAxis = -> Sketch196 [N_Axis]
  Refine = true
  Suppressed = false
  Type = 0
FEATURE [Sketcher::SketchObject] Sketch197
  ArcFitTolerance = 1e-06
  AttachmentSupport = -> [Pad104]
  FullyConstrained = true
  MakeInternals = false
  MapMode = 5
  Placement = pos=(0,0,1.9) rot=(0,0,1;0rad)
  sketch-geometry (4):
    g0: ArcOfCircle CenterX=27.9 CenterY=1.99e-14 CenterZ=0 NormalX=0 NormalY=0 NormalZ=1 AngleXU=0 Radius=2.5 StartAngle=1.5708 EndAngle=4.71239
    g1: ArcOfCircle CenterX=42.05 CenterY=0 CenterZ=0 NormalX=0 NormalY=0 NormalZ=1 AngleXU=0 Radius=2.5 StartAngle=4.71239 EndAngle=7.85398
    g2: LineSegment StartX=27.9 StartY=2.5 StartZ=0 EndX=42.05 EndY=2.5 EndZ=0
    g3: LineSegment StartX=27.9 StartY=-2.5 StartZ=0 EndX=42.05 EndY=-2.5 EndZ=0
  constraints (9):
    c: Tangent(g0,g2) = 1.5708
    c: Tangent(g0,g3) = -1.5708
    c: Tangent(g1,g2) = 1.5708
    c: Tangent(g1,g3) = -1.5708
    c: Equal(g0,g1)
    c: Horizontal(g3)
    c: Coincident(g1,g-3)
    c: Diameter(g0) = 5
    c: DistanceX(g0,g1) = 14.15
FEATURE [PartDesign::Pocket] Pocket097
  BaseFeature = -> Pad104
  Direction = (0,0,-1)
  Length = 2
  Length2 = 5
  Profile = -> Sketch197
  ReferenceAxis = -> Sketch197 [N_Axis]
  Refine = true
  Suppressed = false
  Type = 0
FEATURE [Sketcher::SketchObject] Sketch198
  ArcFitTolerance = 1e-06
  AttachmentSupport = -> [Pocket097]
  ExternalGeometry = -> [Pocket097]
  FullyConstrained = true
  MakeInternals = false
  MapMode = 5
  Placement = pos=(0,0,1.9) rot=(0,0,1;0rad)
  sketch-geometry (8):
    g0: ArcOfCircle CenterX=27.9 CenterY=1.186e-13 CenterZ=0 NormalX=0 NormalY=0 NormalZ=1 AngleXU=0 Radius=2.5 StartAngle=1.57079 EndAngle=4.7124
    g1: ArcOfCircle CenterX=42.05 CenterY=-2e-16 CenterZ=0 NormalX=0 NormalY=0 NormalZ=1 AngleXU=0 Radius=2.5 StartAngle=4.71239 EndAngle=7.85398
    g2: LineSegment StartX=42.05 StartY=2.5 StartZ=0 EndX=27.9 EndY=2.5 EndZ=0
    g3: LineSegment StartX=42.05 StartY=-2.5 StartZ=0 EndX=27.9 EndY=-2.5 EndZ=0
    g4: ArcOfCircle CenterX=42.05 CenterY=1.187e-13 CenterZ=0 NormalX=0 NormalY=0 NormalZ=1 AngleXU=0 Radius=4 StartAngle=4.71239 EndAngle=7.85398
    g5: LineSegment StartX=27.9 StartY=4 StartZ=0 EndX=42.05 EndY=4 EndZ=0
    g6: LineSegment StartX=42.05 StartY=-4 StartZ=0 EndX=27.9 EndY=-4 EndZ=0
    g7: ArcOfCircle CenterX=27.9 CenterY=1.19e-13 CenterZ=0 NormalX=0 NormalY=0 NormalZ=1 AngleXU=0 Radius=4 StartAngle=1.5708 EndAngle=4.71239
  constraints (24):
    c: Coincident(g1,g-6)
    c: Coincident(g1,g-4)
    c: Coincident(g0,g-6)
    c: Coincident(g0,g-5)
    c: Coincident(g3,g0)
    c: Coincident(g2,g0)
    c: Coincident(g2,g1)
    c: Coincident(g3,g1)
    c: Radius(g1) = 2.5
    c: DistanceY(g0,g5) = 1.5
    c: DistanceY(g6,g0) = 1.5
    c: Horizontal(g5)
    c: Horizontal(g6)
    c: Radius(g0) = 2.5
    c: DistanceX(g5,g1) = 0
    c: DistanceX(g1,g6) = 0
    c: DistanceX(g0,g5) = 0
    c: DistanceX(g6,g0) = 0
    c: Coincident(g4,g5)
    c: Coincident(g4,g6)
    c: Radius(g4) = 4
    c: Coincident(g7,g5)
    c: Coincident(g7,g6)
    c: Radius(g7) = 4
FEATURE [PartDesign::Pad] Pad105
  BaseFeature = -> Pocket097
  Direction = (0,0,1)
  Length = 1.5
  Length2 = 10
  Profile = -> Sketch198
  ReferenceAxis = -> Sketch198 [N_Axis]
  Refine = true
  Suppressed = false
  Type = 0
FEATURE [Sketcher::SketchObject] Sketch199
  ArcFitTolerance = 1e-06
  AttachmentSupport = -> [Pad105]
  ExternalGeometry = -> [Pad105]
  FullyConstrained = true
  MakeInternals = false
  MapMode = 5
  Placement = pos=(0,0,0) rot=(1,0,0;3.14159rad)
  sketch-geometry (8):
    g0: ArcOfCircle CenterX=27.9 CenterY=-1.089e-13 CenterZ=0 NormalX=0 NormalY=0 NormalZ=1 AngleXU=0 Radius=2.5 StartAngle=1.5708 EndAngle=4.71239
    g1: ArcOfCircle CenterX=42.05 CenterY=0 CenterZ=0 NormalX=0 NormalY=0 NormalZ=1 AngleXU=0 Radius=2.5 StartAngle=4.71239 EndAngle=7.85398
    g2: LineSegment StartX=27.9 StartY=2.5 StartZ=0 EndX=42.05 EndY=2.5 EndZ=0
    g3: LineSegment StartX=42.05 StartY=-2.5 StartZ=0 EndX=27.9 EndY=-2.5 EndZ=0
    g4: LineSegment StartX=27.9 StartY=4 StartZ=0 EndX=42.05 EndY=4 EndZ=0
    g5: LineSegment StartX=42.05 StartY=-4 StartZ=0 EndX=27.9 EndY=-4 EndZ=0
    g6: ArcOfCircle CenterX=27.9 CenterY=-1.089e-13 CenterZ=0 NormalX=0 NormalY=0 NormalZ=1 AngleXU=0 Radius=4 StartAngle=1.57079 EndAngle=4.7124
    g7: ArcOfCircle CenterX=42.05 CenterY=-1.088e-13 CenterZ=0 NormalX=0 NormalY=0 NormalZ=1 AngleXU=0 Radius=4 StartAngle=4.71239 EndAngle=7.85398
  constraints (22):
    c: Coincident(g0,g-4)
    c: Coincident(g0,g-6)
    c: Tangent(g1,g-5) = -1.5708
    c: Coincident(g1,g-6)
    c: Coincident(g2,g0)
    c: Coincident(g2,g1)
    c: Coincident(g3,g1)
    c: Tangent(g3,g0) = 1.5708
    c: Horizontal(g4)
    c: Horizontal(g5)
    c: Coincident(g6,g4)
    c: Coincident(g6,g5)
    c: Coincident(g7,g4)
    c: Coincident(g7,g5)
    c: DistanceY(g0,g4) = 1.5
    c: DistanceY(g5,g0) = 1.5
    c: Radius(g6) = 4
    c: Radius(g7) = 4
    c: DistanceX(g4,g0) = 0
    c: DistanceX(g1,g4) = 0
    c: DistanceX(g5,g0) = 0
    c: DistanceX(g1,g5) = 0
FEATURE [PartDesign::Pad] Pad106
  BaseFeature = -> Pad105
  Direction = (0,0,-1)
  Length = 1.5
  Length2 = 10
  Profile = -> Sketch199
  ReferenceAxis = -> Sketch199 [N_Axis]
  Refine = true
  Suppressed = false
  Type = 0
FEATURE [Sketcher::SketchObject] Sketch200
  ArcFitTolerance = 1e-06
  AttachmentSupport = -> [Pad106]
  FullyConstrained = true
  MakeInternals = false
  MapMode = 5
  Placement = pos=(0,0,1.9) rot=(0,0,1;0rad)
  sketch-geometry (8):
    g0: ArcOfCircle CenterX=42.05 CenterY=4e-16 CenterZ=0 NormalX=0 NormalY=0 NormalZ=1 AngleXU=0 Radius=5.55 StartAngle=4.71239 EndAngle=7.85398
    g1: ArcOfCircle CenterX=42.05 CenterY=4e-16 CenterZ=0 NormalX=0 NormalY=0 NormalZ=1 AngleXU=0 Radius=7.05 StartAngle=4.71239 EndAngle=7.85398
    g2: LineSegment StartX=42.05 StartY=-7.05 StartZ=0 EndX=19.17 EndY=-7.05 EndZ=0
    g3: LineSegment StartX=19.17 StartY=-7.05 StartZ=0 EndX=19.17 EndY=-5.55 EndZ=0
    g4: LineSegment StartX=19.17 StartY=-5.55 StartZ=0 EndX=42.05 EndY=-5.55 EndZ=0
    g5: LineSegment StartX=42.05 StartY=5.55 StartZ=0 EndX=35.05 EndY=5.55 EndZ=0
    g6: LineSegment StartX=42.05 StartY=7.05 StartZ=0 EndX=35.05 EndY=7.05 EndZ=0
    g7: LineSegment StartX=35.05 StartY=7.05 StartZ=0 EndX=35.05 EndY=5.55 EndZ=0
  constraints (21):
    c: Coincident(g0,g-5)
    c: Tangent(g0,g-4) = -1.5708
    c: Coincident(g2,g1)
    c: Horizontal(g2)
    c: Coincident(g3,g2)
    c: Coincident(g3,g-5)
    c: Vertical(g3)
    c: Coincident(g4,g3)
    c: Coincident(g4,g0)
    c: Coincident(g5,g0)
    c: PointOnObject(g5,g-3)
    c: Coincident(g6,g1)
    c: Horizontal(g6)
    c: Coincident(g7,g6)
    c: Coincident(g7,g5)
    c: Coincident(g1,g0)
    c: DistanceY(g0,g1) = 1.5
    c: Vertical(g7)
    c: DistanceX(g1,g0) = 0
    c: DistanceX(g6,g6) = 7
    c: DistanceX(g1,g0) = 0
FEATURE [PartDesign::Pad] Pad107
  BaseFeature = -> Pad106
  Direction = (0,0,1)
  Length = 4.9
  Length2 = 10
  Profile = -> Sketch200
  ReferenceAxis = -> Sketch200 [N_Axis]
  Refine = true
  Reversed = true
  Suppressed = false
  Type = 0
FEATURE [PartDesign::Pad] Pad108
  BaseFeature = -> Pad107
  Direction = (0,0,1)
  Length = 3.1
  Length2 = 10
  Profile = -> Sketch200
  ReferenceAxis = -> Sketch200 [N_Axis]
  Refine = true
  Suppressed = false
  Type = 0
FEATURE [Sketcher::SketchObject] Sketch201
  ArcFitTolerance = 1e-06
  AttachmentSupport = -> [Pad108]
  ExternalGeometry = -> [Pad108]
  FullyConstrained = true
  MakeInternals = false
  MapMode = 5
  Placement = pos=(0,0,-1.5) rot=(1,0,0;3.14159rad)
  sketch-geometry (4):
    g0: Circle CenterX=27.9 CenterY=4 CenterZ=0 NormalX=0 NormalY=0 NormalZ=1 AngleXU=0 Radius=1
    g1: Circle CenterX=42.05 CenterY=4 CenterZ=0 NormalX=0 NormalY=0 NormalZ=1 AngleXU=0 Radius=1
    g2: Circle CenterX=42.05 CenterY=-4 CenterZ=0 NormalX=0 NormalY=0 NormalZ=1 AngleXU=0 Radius=1
    g3: Circle CenterX=27.9 CenterY=-4 CenterZ=0 NormalX=0 NormalY=0 NormalZ=1 AngleXU=0 Radius=1
  constraints (8):
    c: Diameter(g0) = 2
    c: Coincident(g1,g-3)
    c: Coincident(g2,g-3)
    c: Diameter(g3) = 2
    c: Diameter(g2) = 2
    c: Diameter(g1) = 2
    c: Coincident(g0,g-4)
    c: Coincident(g3,g-5)
FEATURE [Sketcher::SketchObject] Sketch202
  ArcFitTolerance = 1e-06
  FullyConstrained = true
  MakeInternals = false
  MapMode = 5
  Placement = pos=(0,0,-3) rot=(1,0,0;3.14159rad)
  sketch-geometry (26):
    g0: ArcOfCircle CenterX=23.476 CenterY=7.05 CenterZ=0 NormalX=0 NormalY=0 NormalZ=1 AngleXU=0 Radius=0.6 StartAngle=6e-16 EndAngle=3.14159
    g1: ArcOfCircle CenterX=27.376 CenterY=7.05 CenterZ=0 NormalX=0 NormalY=0 NormalZ=1 AngleXU=0 Radius=0.6 StartAngle=6e-16 EndAngle=3.14159
    g2: ArcOfCircle CenterX=31.276 CenterY=7.05 CenterZ=0 NormalX=0 NormalY=0 NormalZ=1 AngleXU=0 Radius=0.6 StartAngle=6e-16 EndAngle=3.14159
    g3: ArcOfCircle CenterX=35.176 CenterY=7.05 CenterZ=0 NormalX=0 NormalY=0 NormalZ=1 AngleXU=0 Radius=0.6 StartAngle=6e-16 EndAngle=3.14159
    g4: ArcOfCircle CenterX=39.076 CenterY=7.05 CenterZ=0 NormalX=0 NormalY=0 NormalZ=1 AngleXU=0 Radius=0.6 StartAngle=6e-16 EndAngle=3.14159
    g5: ArcOfCircle CenterX=49.1 CenterY=0 CenterZ=0 NormalX=0 NormalY=0 NormalZ=1 AngleXU=0 Radius=0.6 StartAngle=4.66982 EndAngle=7.89655
    g6: ArcOfCircle CenterX=47.3516 CenterY=4.64708 CenterZ=0 NormalX=0 NormalY=0 NormalZ=1 AngleXU=0 Radius=0.6 StartAngle=5.38953 EndAngle=8.61625
    g7: ArcOfCircle CenterX=42.9736 CenterY=6.98923 CenterZ=0 NormalX=0 NormalY=0 NormalZ=1 AngleXU=0 Radius=0.6 StartAngle=6.10923 EndAngle=9.33595
    g8: ArcOfCircle CenterX=47.3516 CenterY=-4.64708 CenterZ=0 NormalX=0 NormalY=0 NormalZ=1 AngleXU=0 Radius=0.6 StartAngle=3.95012 EndAngle=7.17685
    g9: ArcOfCircle CenterX=42.9736 CenterY=-6.98923 CenterZ=0 NormalX=0 NormalY=0 NormalZ=1 AngleXU=0 Radius=0.6 StartAngle=3.23042 EndAngle=6.45714
    g10: ArcOfCircle CenterX=39.076 CenterY=-7.05 CenterZ=0 NormalX=0 NormalY=0 NormalZ=1 AngleXU=0 Radius=0.6 StartAngle=3.14159 EndAngle=6.28319
    g11: ArcOfCircle CenterX=19.77 CenterY=7.05 CenterZ=0 NormalX=0 NormalY=0 NormalZ=1 AngleXU=0 Radius=0.6 StartAngle=6e-16 EndAngle=3.14159
    g12: ArcOfCircle CenterX=35.65 CenterY=-7.05 CenterZ=0 NormalX=0 NormalY=0 NormalZ=1 AngleXU=0 Radius=0.6 StartAngle=3.14159 EndAngle=6.28319
    g13: LineSegment StartX=19.17 StartY=7.05 StartZ=0 EndX=20.37 EndY=7.05 EndZ=0
    g14: LineSegment StartX=22.876 StartY=7.05 StartZ=0 EndX=24.076 EndY=7.05 EndZ=0
    g15: LineSegment StartX=26.776 StartY=7.05 StartZ=0 EndX=27.976 EndY=7.05 EndZ=0
    g16: LineSegment StartX=30.676 StartY=7.05 StartZ=0 EndX=31.876 EndY=7.05 EndZ=0
    g17: LineSegment StartX=34.576 StartY=7.05 StartZ=0 EndX=35.776 EndY=7.05 EndZ=0
    g18: LineSegment StartX=38.476 StartY=7.05 StartZ=0 EndX=39.676 EndY=7.05 EndZ=0
    g19: LineSegment StartX=42.376 StartY=7.04246 StartZ=0 EndX=43.5646 EndY=6.88538 EndZ=0
    g20: LineSegment StartX=46.9373 StartY=5.08105 StartZ=0 EndX=47.7276 EndY=4.17946 EndZ=0
    g21: LineSegment StartX=49.0745 StartY=0.599457 StartZ=0 EndX=49.0745 EndY=-0.599457 EndZ=0
    g22: LineSegment StartX=47.7276 StartY=-4.17946 StartZ=0 EndX=46.9373 EndY=-5.08105 EndZ=0
    g23: LineSegment StartX=43.5646 StartY=-6.88538 StartZ=0 EndX=42.376 EndY=-7.04246 EndZ=0
    g24: LineSegment StartX=39.676 StartY=-7.05 StartZ=0 EndX=38.476 EndY=-7.05 EndZ=0
    g25: LineSegment StartX=36.25 StartY=-7.05 StartZ=0 EndX=35.05 EndY=-7.05 EndZ=0
  constraints (89):
    c: PointOnObject(g0,g-3)
    c: PointOnObject(g0,g-3)
    c: PointOnObject(g1,g-3)
    c: PointOnObject(g2,g-3)
    c: PointOnObject(g2,g-3)
    c: PointOnObject(g3,g-3)
    c: PointOnObject(g3,g-3)
    c: PointOnObject(g4,g-3)
    c: PointOnObject(g4,g-3)
    c: Radius(g0) = 0.6
    c: PointOnObject(g0,g-3)
    c: PointOnObject(g1,g-3)
    c: PointOnObject(g1,g-3)
    c: Radius(g1) = 0.6
    c: DistanceX(g0,g1) = 2.7
    c: DistanceX(g1,g2) = 2.7
    c: Radius(g2) = 0.6
    c: PointOnObject(g2,g-3)
    c: Radius(g3) = 0.6
    c: Radius(g4) = 0.6
    c: PointOnObject(g3,g-3)
    c: PointOnObject(g4,g-3)
    c: DistanceX(g2,g3) = 2.7
    c: DistanceX(g3,g4) = 2.7
    c: PointOnObject(g5,g-4)
    c: PointOnObject(g5,g-4)
    c: Radius(g5) = 0.6
    c: PointOnObject(g6,g-4)
    c: PointOnObject(g6,g-4)
    c: PointOnObject(g7,g-4)
    c: PointOnObject(g7,g-4)
    c: PointOnObject(g8,g-4)
    c: PointOnObject(g8,g-4)
    c: PointOnObject(g9,g-4)
    c: PointOnObject(g9,g-4)
    c: PointOnObject(g10,g-5)
    c: PointOnObject(g10,g-5)
    c: PointOnObject(g11,g-3)
    c: Radius(g7) = 0.6
    c: Radius(g6) = 0.6
    c: Radius(g8) = 0.6
    c: Radius(g9) = 0.6
    c: Radius(g10) = 0.6
    c: Radius(g11) = 0.6
    c: PointOnObject(g11,g-3)
    c: PointOnObject(g7,g-4)
    c: PointOnObject(g6,g-4)
    c: PointOnObject(g5,g-4)
    c: PointOnObject(g5,g-1)
    c: PointOnObject(g8,g-4)
    c: PointOnObject(g9,g-4)
    c: PointOnObject(g10,g-5)
    c: Distance(g6,g7) = 3.825
    c: Distance(g5,g6) = 3.825
    c: DistanceX(g4,g7) = 2.7
    c: Coincident(g-3,g11)
    c: Distance(g5,g8) = 3.825
    c: Distance(g8,g9) = 3.825
    c: DistanceX(g10,g9) = 2.7
    c: Coincident(g12,g-5)
    c: PointOnObject(g12,g-5)
    c: PointOnObject(g12,g-5)
    c: Radius(g12) = 0.6
    c: Coincident(g13,g11)
    c: Coincident(g13,g11)
    c: Coincident(g14,g0)
    c: Coincident(g14,g0)
    c: Coincident(g15,g1)
    c: Coincident(g15,g1)
    c: Coincident(g16,g2)
    c: Coincident(g16,g2)
    c: Coincident(g17,g3)
    c: Coincident(g17,g3)
    c: Coincident(g18,g4)
    c: Coincident(g18,g4)
    c: Coincident(g19,g7)
    c: Coincident(g19,g7)
    c: Coincident(g20,g6)
    c: Coincident(g20,g6)
    c: Coincident(g21,g5)
    c: Coincident(g21,g5)
    c: Coincident(g22,g8)
    c: Coincident(g22,g8)
    c: Coincident(g23,g9)
    c: Coincident(g23,g9)
    c: Coincident(g24,g10)
    c: Coincident(g24,g10)
    c: Coincident(g25,g12)
    c: Coincident(g25,g12)
FEATURE [PartDesign::Pad] Pad110
  BaseFeature = -> Pad108
  Direction = (0,-1e-16,-1)
  Length = 8
  Length2 = 10
  Profile = -> Sketch202
  ReferenceAxis = -> Sketch202 [N_Axis]
  Refine = true
  Reversed = true
  Suppressed = false
  Type = 0
FEATURE [PartDesign::Pad] Pad160
  BaseFeature = -> Pad110
  Direction = (0,0,-1)
  Length = 2
  Length2 = 10
  Profile = -> Sketch201
  ReferenceAxis = -> Sketch201 [N_Axis]
  Refine = true
  Reversed = true
  Suppressed = false
  Type = 0
FEATURE [PartDesign::Body] Body016  label="Right_Foot"
  AllowCompound = false
  Group = -> [Sketch196,Pad104,Sketch197,Pocket097,Sketch198,Pad105,Sketch199,Pad106,Sketch200,Pad107,Pad108,Sketch201,Sketch202,Pad110,Pad160]
  Origin = -> Origin018
  Placement = pos=(24.7,-51,-6.5) rot=(0.57735,0.57735,-0.57735;4.18879rad)
  Tip = -> Pad160
